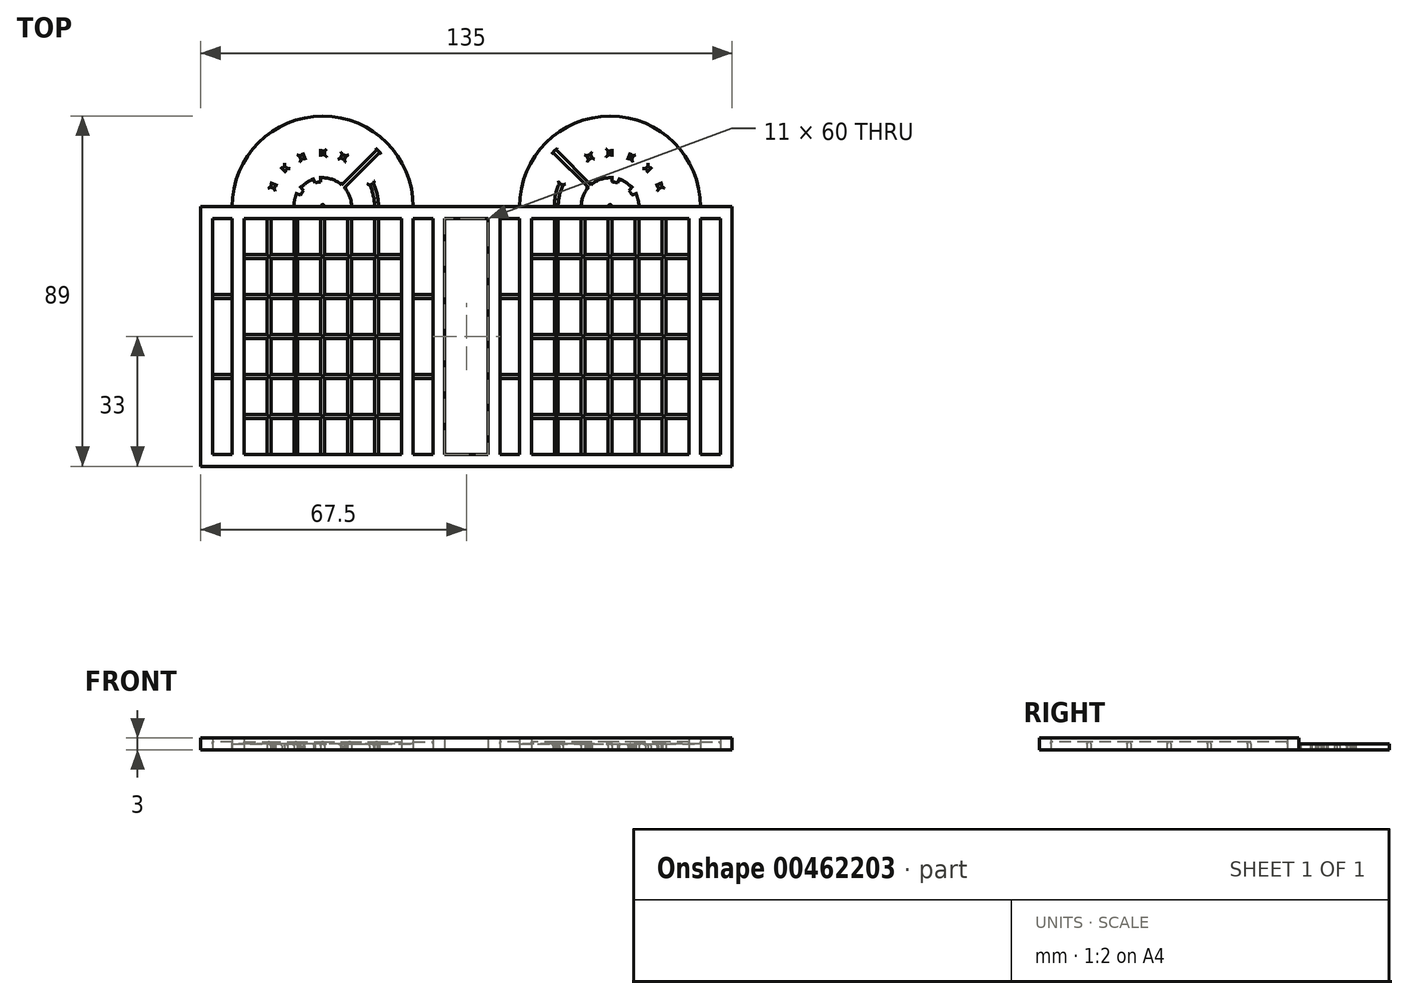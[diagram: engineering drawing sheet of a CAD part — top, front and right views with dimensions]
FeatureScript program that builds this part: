
annotation { "Feature Type Name" : "Feature", "Feature Type Description" : "" }
export const myFeature = defineFeature(function(context is Context, id is Id, definition is map)
    precondition{}
    {
        {
            var Q0;
            Q0=qCreatedBy(makeId("Top.planeOp"),FACE);
            var sketch = newSketch(context, id + "F0", { "sketchPlane" : qUnion([Q0])});
            skLineSegment(sketch, "E0.bottom", {"start": v(0, 0) * mm, "end": v(62, 0) * mm});
            skLineSegment(sketch, "E0.top", {"start": v(0, 60) * mm, "end": v(62, 60) * mm});
            skLineSegment(sketch, "E0.left", {"start": v(0, 0) * mm, "end": v(0, 60) * mm});
            skLineSegment(sketch, "E0.right", {"start": v(62, 0) * mm, "end": v(62, 60) * mm});
            skLineSegment(sketch, "E1", {"start": v(0, 0) * mm, "end": v(8, 0) * mm, "construction": true});
            skLineSegment(sketch, "E2", {"start": v(62, 0) * mm, "end": v(54, 0) * mm, "construction": true});
            skLineSegment(sketch, "E3", {"start": v(62, 0) * mm, "end": v(59, 0) * mm, "construction": true});
            skLineSegment(sketch, "E4", {"start": v(59, 0) * mm, "end": v(59, 60) * mm});
            skLineSegment(sketch, "E5", {"start": v(0, 60) * mm, "end": v(3, 60) * mm, "construction": true});
            skLineSegment(sketch, "E6", {"start": v(3, 60) * mm, "end": v(3, 0) * mm});
            skLineSegment(sketch, "E7", {"start": v(8, 0) * mm, "end": v(8, 60) * mm});
            skLineSegment(sketch, "E8", {"start": v(54, 0) * mm, "end": v(54, 60) * mm});
            skLineSegment(sketch, "E9", {"start": v(8, 0) * mm, "end": v(11, 0) * mm, "construction": true});
            skLineSegment(sketch, "E10", {"start": v(54, 0) * mm, "end": v(51, 0) * mm, "construction": true});
            skLineSegment(sketch, "E11", {"start": v(11, 0) * mm, "end": v(11, 60) * mm});
            skLineSegment(sketch, "E12", {"start": v(51, 0) * mm, "end": v(51, 60) * mm});
            skLineSegment(sketch, "E13.bottom", {"start": v(51, 0) * mm, "end": v(45.17, 0) * mm});
            skLineSegment(sketch, "E13.top", {"start": v(51, 9.17) * mm, "end": v(45.17, 9.17) * mm});
            skLineSegment(sketch, "E13.left", {"start": v(51, 0) * mm, "end": v(51, 9.17) * mm});
            skLineSegment(sketch, "E13.right", {"start": v(45.17, 0) * mm, "end": v(45.17, 9.17) * mm});
            skLineSegment(sketch, "E14.bottom", {"start": v(45.17, 0) * mm, "end": v(44.17, 0) * mm});
            skLineSegment(sketch, "E14.top", {"start": v(45.17, 9.17) * mm, "end": v(44.17, 9.17) * mm, "construction": true});
            skLineSegment(sketch, "E14.right", {"start": v(44.17, 0) * mm, "end": v(44.17, 9.17) * mm});
            skLineSegment(sketch, "E15.top", {"start": v(51, 10.17) * mm, "end": v(45.17, 10.17) * mm});
            skLineSegment(sketch, "E15.left", {"start": v(51, 9.17) * mm, "end": v(51, 10.17) * mm});
            skLineSegment(sketch, "E15.right", {"start": v(45.17, 9.17) * mm, "end": v(45.17, 10.17) * mm, "construction": true});
            skLineSegment(sketch, "E16", {"start": v(44.17, 9.17) * mm, "end": v(44.17, 10.17) * mm, "construction": true});
            skLineSegment(sketch, "E17", {"start": v(44.17, 10.17) * mm, "end": v(45.17, 10.17) * mm, "construction": true});
            skLineSegment(sketch, "E18.0.1.0", {"start": v(44.17, 20.33) * mm, "end": v(45.17, 20.33) * mm, "construction": true});
            skLineSegment(sketch, "E18.0.1.1", {"start": v(51, 20.33) * mm, "end": v(45.17, 20.33) * mm});
            skLineSegment(sketch, "E18.0.1.2", {"start": v(51, 19.33) * mm, "end": v(45.17, 19.33) * mm});
            skLineSegment(sketch, "E18.0.1.3", {"start": v(45.17, 10.17) * mm, "end": v(45.17, 19.33) * mm});
            skLineSegment(sketch, "E18.0.1.4", {"start": v(44.17, 10.17) * mm, "end": v(44.17, 19.33) * mm});
            skLineSegment(sketch, "E18.0.1.5", {"start": v(45.17, 19.33) * mm, "end": v(44.17, 19.33) * mm, "construction": true});
            skLineSegment(sketch, "E18.0.1.6", {"start": v(44.17, 19.33) * mm, "end": v(44.17, 20.33) * mm, "construction": true});
            skLineSegment(sketch, "E18.0.1.7", {"start": v(45.17, 19.33) * mm, "end": v(45.17, 20.33) * mm, "construction": true});
            skLineSegment(sketch, "E18.0.2.0", {"start": v(44.17, 30.5) * mm, "end": v(45.17, 30.5) * mm, "construction": true});
            skLineSegment(sketch, "E18.0.2.1", {"start": v(51, 30.5) * mm, "end": v(45.17, 30.5) * mm});
            skLineSegment(sketch, "E18.0.2.2", {"start": v(51, 29.5) * mm, "end": v(45.17, 29.5) * mm});
            skLineSegment(sketch, "E18.0.2.3", {"start": v(45.17, 20.33) * mm, "end": v(45.17, 29.5) * mm});
            skLineSegment(sketch, "E18.0.2.4", {"start": v(44.17, 20.33) * mm, "end": v(44.17, 29.5) * mm});
            skLineSegment(sketch, "E18.0.2.5", {"start": v(45.17, 29.5) * mm, "end": v(44.17, 29.5) * mm, "construction": true});
            skLineSegment(sketch, "E18.0.2.6", {"start": v(44.17, 29.5) * mm, "end": v(44.17, 30.5) * mm, "construction": true});
            skLineSegment(sketch, "E18.0.2.7", {"start": v(45.17, 29.5) * mm, "end": v(45.17, 30.5) * mm, "construction": true});
            skLineSegment(sketch, "E18.0.3.0", {"start": v(44.17, 40.67) * mm, "end": v(45.17, 40.67) * mm, "construction": true});
            skLineSegment(sketch, "E18.0.3.1", {"start": v(51, 40.67) * mm, "end": v(45.17, 40.67) * mm});
            skLineSegment(sketch, "E18.0.3.2", {"start": v(51, 39.67) * mm, "end": v(45.17, 39.67) * mm});
            skLineSegment(sketch, "E18.0.3.3", {"start": v(45.17, 30.5) * mm, "end": v(45.17, 39.67) * mm});
            skLineSegment(sketch, "E18.0.3.4", {"start": v(44.17, 30.5) * mm, "end": v(44.17, 39.67) * mm});
            skLineSegment(sketch, "E18.0.3.5", {"start": v(45.17, 39.67) * mm, "end": v(44.17, 39.67) * mm, "construction": true});
            skLineSegment(sketch, "E18.0.3.6", {"start": v(44.17, 39.67) * mm, "end": v(44.17, 40.67) * mm, "construction": true});
            skLineSegment(sketch, "E18.0.3.7", {"start": v(45.17, 39.67) * mm, "end": v(45.17, 40.67) * mm, "construction": true});
            skLineSegment(sketch, "E18.0.4.0", {"start": v(44.17, 50.83) * mm, "end": v(45.17, 50.83) * mm, "construction": true});
            skLineSegment(sketch, "E18.0.4.1", {"start": v(51, 50.83) * mm, "end": v(45.17, 50.83) * mm});
            skLineSegment(sketch, "E18.0.4.2", {"start": v(51, 49.83) * mm, "end": v(45.17, 49.83) * mm});
            skLineSegment(sketch, "E18.0.4.3", {"start": v(45.17, 40.67) * mm, "end": v(45.17, 49.83) * mm});
            skLineSegment(sketch, "E18.0.4.4", {"start": v(44.17, 40.67) * mm, "end": v(44.17, 49.83) * mm});
            skLineSegment(sketch, "E18.0.4.5", {"start": v(45.17, 49.83) * mm, "end": v(44.17, 49.83) * mm, "construction": true});
            skLineSegment(sketch, "E18.0.4.6", {"start": v(44.17, 49.83) * mm, "end": v(44.17, 50.83) * mm, "construction": true});
            skLineSegment(sketch, "E18.0.4.7", {"start": v(45.17, 49.83) * mm, "end": v(45.17, 50.83) * mm, "construction": true});
            skLineSegment(sketch, "E18.0.5.2", {"start": v(51, 60) * mm, "end": v(45.17, 60) * mm});
            skLineSegment(sketch, "E18.0.5.3", {"start": v(45.17, 50.83) * mm, "end": v(45.17, 60) * mm});
            skLineSegment(sketch, "E18.0.5.4", {"start": v(44.17, 50.83) * mm, "end": v(44.17, 60) * mm});
            skLineSegment(sketch, "E18.0.5.5", {"start": v(45.17, 60) * mm, "end": v(44.17, 60) * mm, "construction": true});
            skLineSegment(sketch, "E18.1.0.0", {"start": v(37.33, 10.17) * mm, "end": v(38.33, 10.17) * mm, "construction": true});
            skLineSegment(sketch, "E18.1.0.1", {"start": v(44.17, 10.17) * mm, "end": v(38.33, 10.17) * mm});
            skLineSegment(sketch, "E18.1.0.2", {"start": v(44.17, 9.17) * mm, "end": v(38.33, 9.17) * mm});
            skLineSegment(sketch, "E18.1.0.3", {"start": v(38.33, 0) * mm, "end": v(38.33, 9.17) * mm});
            skLineSegment(sketch, "E18.1.0.4", {"start": v(37.33, 0) * mm, "end": v(37.33, 9.17) * mm});
            skLineSegment(sketch, "E18.1.0.5", {"start": v(38.33, 9.17) * mm, "end": v(37.33, 9.17) * mm, "construction": true});
            skLineSegment(sketch, "E18.1.0.6", {"start": v(37.33, 9.17) * mm, "end": v(37.33, 10.17) * mm, "construction": true});
            skLineSegment(sketch, "E18.1.0.7", {"start": v(38.33, 9.17) * mm, "end": v(38.33, 10.17) * mm, "construction": true});
            skLineSegment(sketch, "E18.1.1.0", {"start": v(37.33, 20.33) * mm, "end": v(38.33, 20.33) * mm, "construction": true});
            skLineSegment(sketch, "E18.1.1.1", {"start": v(44.17, 20.33) * mm, "end": v(38.33, 20.33) * mm});
            skLineSegment(sketch, "E18.1.1.2", {"start": v(44.17, 19.33) * mm, "end": v(38.33, 19.33) * mm});
            skLineSegment(sketch, "E18.1.1.3", {"start": v(38.33, 10.17) * mm, "end": v(38.33, 19.33) * mm});
            skLineSegment(sketch, "E18.1.1.4", {"start": v(37.33, 10.17) * mm, "end": v(37.33, 19.33) * mm});
            skLineSegment(sketch, "E18.1.1.5", {"start": v(38.33, 19.33) * mm, "end": v(37.33, 19.33) * mm, "construction": true});
            skLineSegment(sketch, "E18.1.1.6", {"start": v(37.33, 19.33) * mm, "end": v(37.33, 20.33) * mm, "construction": true});
            skLineSegment(sketch, "E18.1.1.7", {"start": v(38.33, 19.33) * mm, "end": v(38.33, 20.33) * mm, "construction": true});
            skLineSegment(sketch, "E18.1.2.0", {"start": v(37.33, 30.5) * mm, "end": v(38.33, 30.5) * mm, "construction": true});
            skLineSegment(sketch, "E18.1.2.1", {"start": v(44.17, 30.5) * mm, "end": v(38.33, 30.5) * mm});
            skLineSegment(sketch, "E18.1.2.2", {"start": v(44.17, 29.5) * mm, "end": v(38.33, 29.5) * mm});
            skLineSegment(sketch, "E18.1.2.3", {"start": v(38.33, 20.33) * mm, "end": v(38.33, 29.5) * mm});
            skLineSegment(sketch, "E18.1.2.4", {"start": v(37.33, 20.33) * mm, "end": v(37.33, 29.5) * mm});
            skLineSegment(sketch, "E18.1.2.5", {"start": v(38.33, 29.5) * mm, "end": v(37.33, 29.5) * mm, "construction": true});
            skLineSegment(sketch, "E18.1.2.6", {"start": v(37.33, 29.5) * mm, "end": v(37.33, 30.5) * mm, "construction": true});
            skLineSegment(sketch, "E18.1.2.7", {"start": v(38.33, 29.5) * mm, "end": v(38.33, 30.5) * mm, "construction": true});
            skLineSegment(sketch, "E18.1.3.0", {"start": v(37.33, 40.67) * mm, "end": v(38.33, 40.67) * mm, "construction": true});
            skLineSegment(sketch, "E18.1.3.1", {"start": v(44.17, 40.67) * mm, "end": v(38.33, 40.67) * mm});
            skLineSegment(sketch, "E18.1.3.2", {"start": v(44.17, 39.67) * mm, "end": v(38.33, 39.67) * mm});
            skLineSegment(sketch, "E18.1.3.3", {"start": v(38.33, 30.5) * mm, "end": v(38.33, 39.67) * mm});
            skLineSegment(sketch, "E18.1.3.4", {"start": v(37.33, 30.5) * mm, "end": v(37.33, 39.67) * mm});
            skLineSegment(sketch, "E18.1.3.5", {"start": v(38.33, 39.67) * mm, "end": v(37.33, 39.67) * mm, "construction": true});
            skLineSegment(sketch, "E18.1.3.6", {"start": v(37.33, 39.67) * mm, "end": v(37.33, 40.67) * mm, "construction": true});
            skLineSegment(sketch, "E18.1.3.7", {"start": v(38.33, 39.67) * mm, "end": v(38.33, 40.67) * mm, "construction": true});
            skLineSegment(sketch, "E18.1.4.0", {"start": v(37.33, 50.83) * mm, "end": v(38.33, 50.83) * mm, "construction": true});
            skLineSegment(sketch, "E18.1.4.1", {"start": v(44.17, 50.83) * mm, "end": v(38.33, 50.83) * mm});
            skLineSegment(sketch, "E18.1.4.2", {"start": v(44.17, 49.83) * mm, "end": v(38.33, 49.83) * mm});
            skLineSegment(sketch, "E18.1.4.3", {"start": v(38.33, 40.67) * mm, "end": v(38.33, 49.83) * mm});
            skLineSegment(sketch, "E18.1.4.4", {"start": v(37.33, 40.67) * mm, "end": v(37.33, 49.83) * mm});
            skLineSegment(sketch, "E18.1.4.5", {"start": v(38.33, 49.83) * mm, "end": v(37.33, 49.83) * mm, "construction": true});
            skLineSegment(sketch, "E18.1.4.6", {"start": v(37.33, 49.83) * mm, "end": v(37.33, 50.83) * mm, "construction": true});
            skLineSegment(sketch, "E18.1.4.7", {"start": v(38.33, 49.83) * mm, "end": v(38.33, 50.83) * mm, "construction": true});
            skLineSegment(sketch, "E18.1.5.2", {"start": v(44.17, 60) * mm, "end": v(38.33, 60) * mm});
            skLineSegment(sketch, "E18.1.5.3", {"start": v(38.33, 50.83) * mm, "end": v(38.33, 60) * mm});
            skLineSegment(sketch, "E18.1.5.4", {"start": v(37.33, 50.83) * mm, "end": v(37.33, 60) * mm});
            skLineSegment(sketch, "E18.1.5.5", {"start": v(38.33, 60) * mm, "end": v(37.33, 60) * mm, "construction": true});
            skLineSegment(sketch, "E18.2.0.0", {"start": v(30.5, 10.17) * mm, "end": v(31.5, 10.17) * mm, "construction": true});
            skLineSegment(sketch, "E18.2.0.1", {"start": v(37.33, 10.17) * mm, "end": v(31.5, 10.17) * mm});
            skLineSegment(sketch, "E18.2.0.2", {"start": v(37.33, 9.17) * mm, "end": v(31.5, 9.17) * mm});
            skLineSegment(sketch, "E18.2.0.3", {"start": v(31.5, 0) * mm, "end": v(31.5, 9.17) * mm});
            skLineSegment(sketch, "E18.2.0.4", {"start": v(30.5, 0) * mm, "end": v(30.5, 9.17) * mm});
            skLineSegment(sketch, "E18.2.0.5", {"start": v(31.5, 9.17) * mm, "end": v(30.5, 9.17) * mm, "construction": true});
            skLineSegment(sketch, "E18.2.0.6", {"start": v(30.5, 9.17) * mm, "end": v(30.5, 10.17) * mm, "construction": true});
            skLineSegment(sketch, "E18.2.0.7", {"start": v(31.5, 9.17) * mm, "end": v(31.5, 10.17) * mm, "construction": true});
            skLineSegment(sketch, "E18.2.1.0", {"start": v(30.5, 20.33) * mm, "end": v(31.5, 20.33) * mm, "construction": true});
            skLineSegment(sketch, "E18.2.1.1", {"start": v(37.33, 20.33) * mm, "end": v(31.5, 20.33) * mm});
            skLineSegment(sketch, "E18.2.1.2", {"start": v(37.33, 19.33) * mm, "end": v(31.5, 19.33) * mm});
            skLineSegment(sketch, "E18.2.1.3", {"start": v(31.5, 10.17) * mm, "end": v(31.5, 19.33) * mm});
            skLineSegment(sketch, "E18.2.1.4", {"start": v(30.5, 10.17) * mm, "end": v(30.5, 19.33) * mm});
            skLineSegment(sketch, "E18.2.1.5", {"start": v(31.5, 19.33) * mm, "end": v(30.5, 19.33) * mm, "construction": true});
            skLineSegment(sketch, "E18.2.1.6", {"start": v(30.5, 19.33) * mm, "end": v(30.5, 20.33) * mm, "construction": true});
            skLineSegment(sketch, "E18.2.1.7", {"start": v(31.5, 19.33) * mm, "end": v(31.5, 20.33) * mm, "construction": true});
            skLineSegment(sketch, "E18.2.2.0", {"start": v(30.5, 30.5) * mm, "end": v(31.5, 30.5) * mm, "construction": true});
            skLineSegment(sketch, "E18.2.2.1", {"start": v(37.33, 30.5) * mm, "end": v(31.5, 30.5) * mm});
            skLineSegment(sketch, "E18.2.2.2", {"start": v(37.33, 29.5) * mm, "end": v(31.5, 29.5) * mm});
            skLineSegment(sketch, "E18.2.2.3", {"start": v(31.5, 20.33) * mm, "end": v(31.5, 29.5) * mm});
            skLineSegment(sketch, "E18.2.2.4", {"start": v(30.5, 20.33) * mm, "end": v(30.5, 29.5) * mm});
            skLineSegment(sketch, "E18.2.2.5", {"start": v(31.5, 29.5) * mm, "end": v(30.5, 29.5) * mm, "construction": true});
            skLineSegment(sketch, "E18.2.2.6", {"start": v(30.5, 29.5) * mm, "end": v(30.5, 30.5) * mm, "construction": true});
            skLineSegment(sketch, "E18.2.2.7", {"start": v(31.5, 29.5) * mm, "end": v(31.5, 30.5) * mm, "construction": true});
            skLineSegment(sketch, "E18.2.3.0", {"start": v(30.5, 40.67) * mm, "end": v(31.5, 40.67) * mm, "construction": true});
            skLineSegment(sketch, "E18.2.3.1", {"start": v(37.33, 40.67) * mm, "end": v(31.5, 40.67) * mm});
            skLineSegment(sketch, "E18.2.3.2", {"start": v(37.33, 39.67) * mm, "end": v(31.5, 39.67) * mm});
            skLineSegment(sketch, "E18.2.3.3", {"start": v(31.5, 30.5) * mm, "end": v(31.5, 39.67) * mm});
            skLineSegment(sketch, "E18.2.3.4", {"start": v(30.5, 30.5) * mm, "end": v(30.5, 39.67) * mm});
            skLineSegment(sketch, "E18.2.3.5", {"start": v(31.5, 39.67) * mm, "end": v(30.5, 39.67) * mm, "construction": true});
            skLineSegment(sketch, "E18.2.3.6", {"start": v(30.5, 39.67) * mm, "end": v(30.5, 40.67) * mm, "construction": true});
            skLineSegment(sketch, "E18.2.3.7", {"start": v(31.5, 39.67) * mm, "end": v(31.5, 40.67) * mm, "construction": true});
            skLineSegment(sketch, "E18.2.4.0", {"start": v(30.5, 50.83) * mm, "end": v(31.5, 50.83) * mm, "construction": true});
            skLineSegment(sketch, "E18.2.4.1", {"start": v(37.33, 50.83) * mm, "end": v(31.5, 50.83) * mm});
            skLineSegment(sketch, "E18.2.4.2", {"start": v(37.33, 49.83) * mm, "end": v(31.5, 49.83) * mm});
            skLineSegment(sketch, "E18.2.4.3", {"start": v(31.5, 40.67) * mm, "end": v(31.5, 49.83) * mm});
            skLineSegment(sketch, "E18.2.4.4", {"start": v(30.5, 40.67) * mm, "end": v(30.5, 49.83) * mm});
            skLineSegment(sketch, "E18.2.4.5", {"start": v(31.5, 49.83) * mm, "end": v(30.5, 49.83) * mm, "construction": true});
            skLineSegment(sketch, "E18.2.4.6", {"start": v(30.5, 49.83) * mm, "end": v(30.5, 50.83) * mm, "construction": true});
            skLineSegment(sketch, "E18.2.4.7", {"start": v(31.5, 49.83) * mm, "end": v(31.5, 50.83) * mm, "construction": true});
            skLineSegment(sketch, "E18.2.5.2", {"start": v(37.33, 60) * mm, "end": v(31.5, 60) * mm});
            skLineSegment(sketch, "E18.2.5.3", {"start": v(31.5, 50.83) * mm, "end": v(31.5, 60) * mm});
            skLineSegment(sketch, "E18.2.5.4", {"start": v(30.5, 50.83) * mm, "end": v(30.5, 60) * mm});
            skLineSegment(sketch, "E18.2.5.5", {"start": v(31.5, 60) * mm, "end": v(30.5, 60) * mm, "construction": true});
            skLineSegment(sketch, "E18.3.0.0", {"start": v(23.67, 10.17) * mm, "end": v(24.67, 10.17) * mm, "construction": true});
            skLineSegment(sketch, "E18.3.0.1", {"start": v(30.5, 10.17) * mm, "end": v(24.67, 10.17) * mm});
            skLineSegment(sketch, "E18.3.0.2", {"start": v(30.5, 9.17) * mm, "end": v(24.67, 9.17) * mm});
            skLineSegment(sketch, "E18.3.0.3", {"start": v(24.67, 0) * mm, "end": v(24.67, 9.17) * mm});
            skLineSegment(sketch, "E18.3.0.4", {"start": v(23.67, 0) * mm, "end": v(23.67, 9.17) * mm});
            skLineSegment(sketch, "E18.3.0.5", {"start": v(24.67, 9.17) * mm, "end": v(23.67, 9.17) * mm, "construction": true});
            skLineSegment(sketch, "E18.3.0.6", {"start": v(23.67, 9.17) * mm, "end": v(23.67, 10.17) * mm, "construction": true});
            skLineSegment(sketch, "E18.3.0.7", {"start": v(24.67, 9.17) * mm, "end": v(24.67, 10.17) * mm, "construction": true});
            skLineSegment(sketch, "E18.3.1.0", {"start": v(23.67, 20.33) * mm, "end": v(24.67, 20.33) * mm, "construction": true});
            skLineSegment(sketch, "E18.3.1.1", {"start": v(30.5, 20.33) * mm, "end": v(24.67, 20.33) * mm});
            skLineSegment(sketch, "E18.3.1.2", {"start": v(30.5, 19.33) * mm, "end": v(24.67, 19.33) * mm});
            skLineSegment(sketch, "E18.3.1.3", {"start": v(24.67, 10.17) * mm, "end": v(24.67, 19.33) * mm});
            skLineSegment(sketch, "E18.3.1.4", {"start": v(23.67, 10.17) * mm, "end": v(23.67, 19.33) * mm});
            skLineSegment(sketch, "E18.3.1.5", {"start": v(24.67, 19.33) * mm, "end": v(23.67, 19.33) * mm, "construction": true});
            skLineSegment(sketch, "E18.3.1.6", {"start": v(23.67, 19.33) * mm, "end": v(23.67, 20.33) * mm, "construction": true});
            skLineSegment(sketch, "E18.3.1.7", {"start": v(24.67, 19.33) * mm, "end": v(24.67, 20.33) * mm, "construction": true});
            skLineSegment(sketch, "E18.3.2.0", {"start": v(23.67, 30.5) * mm, "end": v(24.67, 30.5) * mm, "construction": true});
            skLineSegment(sketch, "E18.3.2.1", {"start": v(30.5, 30.5) * mm, "end": v(24.67, 30.5) * mm});
            skLineSegment(sketch, "E18.3.2.2", {"start": v(30.5, 29.5) * mm, "end": v(24.67, 29.5) * mm});
            skLineSegment(sketch, "E18.3.2.3", {"start": v(24.67, 20.33) * mm, "end": v(24.67, 29.5) * mm});
            skLineSegment(sketch, "E18.3.2.4", {"start": v(23.67, 20.33) * mm, "end": v(23.67, 29.5) * mm});
            skLineSegment(sketch, "E18.3.2.5", {"start": v(24.67, 29.5) * mm, "end": v(23.67, 29.5) * mm, "construction": true});
            skLineSegment(sketch, "E18.3.2.6", {"start": v(23.67, 29.5) * mm, "end": v(23.67, 30.5) * mm, "construction": true});
            skLineSegment(sketch, "E18.3.2.7", {"start": v(24.67, 29.5) * mm, "end": v(24.67, 30.5) * mm, "construction": true});
            skLineSegment(sketch, "E18.3.3.0", {"start": v(23.67, 40.67) * mm, "end": v(24.67, 40.67) * mm, "construction": true});
            skLineSegment(sketch, "E18.3.3.1", {"start": v(30.5, 40.67) * mm, "end": v(24.67, 40.67) * mm});
            skLineSegment(sketch, "E18.3.3.2", {"start": v(30.5, 39.67) * mm, "end": v(24.67, 39.67) * mm});
            skLineSegment(sketch, "E18.3.3.3", {"start": v(24.67, 30.5) * mm, "end": v(24.67, 39.67) * mm});
            skLineSegment(sketch, "E18.3.3.4", {"start": v(23.67, 30.5) * mm, "end": v(23.67, 39.67) * mm});
            skLineSegment(sketch, "E18.3.3.5", {"start": v(24.67, 39.67) * mm, "end": v(23.67, 39.67) * mm, "construction": true});
            skLineSegment(sketch, "E18.3.3.6", {"start": v(23.67, 39.67) * mm, "end": v(23.67, 40.67) * mm, "construction": true});
            skLineSegment(sketch, "E18.3.3.7", {"start": v(24.67, 39.67) * mm, "end": v(24.67, 40.67) * mm, "construction": true});
            skLineSegment(sketch, "E18.3.4.0", {"start": v(23.67, 50.83) * mm, "end": v(24.67, 50.83) * mm, "construction": true});
            skLineSegment(sketch, "E18.3.4.1", {"start": v(30.5, 50.83) * mm, "end": v(24.67, 50.83) * mm});
            skLineSegment(sketch, "E18.3.4.2", {"start": v(30.5, 49.83) * mm, "end": v(24.67, 49.83) * mm});
            skLineSegment(sketch, "E18.3.4.3", {"start": v(24.67, 40.67) * mm, "end": v(24.67, 49.83) * mm});
            skLineSegment(sketch, "E18.3.4.4", {"start": v(23.67, 40.67) * mm, "end": v(23.67, 49.83) * mm});
            skLineSegment(sketch, "E18.3.4.5", {"start": v(24.67, 49.83) * mm, "end": v(23.67, 49.83) * mm, "construction": true});
            skLineSegment(sketch, "E18.3.4.6", {"start": v(23.67, 49.83) * mm, "end": v(23.67, 50.83) * mm, "construction": true});
            skLineSegment(sketch, "E18.3.4.7", {"start": v(24.67, 49.83) * mm, "end": v(24.67, 50.83) * mm, "construction": true});
            skLineSegment(sketch, "E18.3.5.2", {"start": v(30.5, 60) * mm, "end": v(24.67, 60) * mm});
            skLineSegment(sketch, "E18.3.5.3", {"start": v(24.67, 50.83) * mm, "end": v(24.67, 60) * mm});
            skLineSegment(sketch, "E18.3.5.4", {"start": v(23.67, 50.83) * mm, "end": v(23.67, 60) * mm});
            skLineSegment(sketch, "E18.3.5.5", {"start": v(24.67, 60) * mm, "end": v(23.67, 60) * mm, "construction": true});
            skLineSegment(sketch, "E18.4.0.0", {"start": v(16.83, 10.17) * mm, "end": v(17.83, 10.17) * mm, "construction": true});
            skLineSegment(sketch, "E18.4.0.1", {"start": v(23.67, 10.17) * mm, "end": v(17.83, 10.17) * mm});
            skLineSegment(sketch, "E18.4.0.2", {"start": v(23.67, 9.17) * mm, "end": v(17.83, 9.17) * mm});
            skLineSegment(sketch, "E18.4.0.3", {"start": v(17.83, 0) * mm, "end": v(17.83, 9.17) * mm});
            skLineSegment(sketch, "E18.4.0.4", {"start": v(16.83, 0) * mm, "end": v(16.83, 9.17) * mm});
            skLineSegment(sketch, "E18.4.0.5", {"start": v(17.83, 9.17) * mm, "end": v(16.83, 9.17) * mm, "construction": true});
            skLineSegment(sketch, "E18.4.0.6", {"start": v(16.83, 9.17) * mm, "end": v(16.83, 10.17) * mm, "construction": true});
            skLineSegment(sketch, "E18.4.0.7", {"start": v(17.83, 9.17) * mm, "end": v(17.83, 10.17) * mm, "construction": true});
            skLineSegment(sketch, "E18.4.1.0", {"start": v(16.83, 20.33) * mm, "end": v(17.83, 20.33) * mm, "construction": true});
            skLineSegment(sketch, "E18.4.1.1", {"start": v(23.67, 20.33) * mm, "end": v(17.83, 20.33) * mm});
            skLineSegment(sketch, "E18.4.1.2", {"start": v(23.67, 19.33) * mm, "end": v(17.83, 19.33) * mm});
            skLineSegment(sketch, "E18.4.1.3", {"start": v(17.83, 10.17) * mm, "end": v(17.83, 19.33) * mm});
            skLineSegment(sketch, "E18.4.1.4", {"start": v(16.83, 10.17) * mm, "end": v(16.83, 19.33) * mm});
            skLineSegment(sketch, "E18.4.1.5", {"start": v(17.83, 19.33) * mm, "end": v(16.83, 19.33) * mm, "construction": true});
            skLineSegment(sketch, "E18.4.1.6", {"start": v(16.83, 19.33) * mm, "end": v(16.83, 20.33) * mm, "construction": true});
            skLineSegment(sketch, "E18.4.1.7", {"start": v(17.83, 19.33) * mm, "end": v(17.83, 20.33) * mm, "construction": true});
            skLineSegment(sketch, "E18.4.2.0", {"start": v(16.83, 30.5) * mm, "end": v(17.83, 30.5) * mm, "construction": true});
            skLineSegment(sketch, "E18.4.2.1", {"start": v(23.67, 30.5) * mm, "end": v(17.83, 30.5) * mm});
            skLineSegment(sketch, "E18.4.2.2", {"start": v(23.67, 29.5) * mm, "end": v(17.83, 29.5) * mm});
            skLineSegment(sketch, "E18.4.2.3", {"start": v(17.83, 20.33) * mm, "end": v(17.83, 29.5) * mm});
            skLineSegment(sketch, "E18.4.2.4", {"start": v(16.83, 20.33) * mm, "end": v(16.83, 29.5) * mm});
            skLineSegment(sketch, "E18.4.2.5", {"start": v(17.83, 29.5) * mm, "end": v(16.83, 29.5) * mm, "construction": true});
            skLineSegment(sketch, "E18.4.2.6", {"start": v(16.83, 29.5) * mm, "end": v(16.83, 30.5) * mm, "construction": true});
            skLineSegment(sketch, "E18.4.2.7", {"start": v(17.83, 29.5) * mm, "end": v(17.83, 30.5) * mm, "construction": true});
            skLineSegment(sketch, "E18.4.3.0", {"start": v(16.83, 40.67) * mm, "end": v(17.83, 40.67) * mm, "construction": true});
            skLineSegment(sketch, "E18.4.3.1", {"start": v(23.67, 40.67) * mm, "end": v(17.83, 40.67) * mm});
            skLineSegment(sketch, "E18.4.3.2", {"start": v(23.67, 39.67) * mm, "end": v(17.83, 39.67) * mm});
            skLineSegment(sketch, "E18.4.3.3", {"start": v(17.83, 30.5) * mm, "end": v(17.83, 39.67) * mm});
            skLineSegment(sketch, "E18.4.3.4", {"start": v(16.83, 30.5) * mm, "end": v(16.83, 39.67) * mm});
            skLineSegment(sketch, "E18.4.3.5", {"start": v(17.83, 39.67) * mm, "end": v(16.83, 39.67) * mm, "construction": true});
            skLineSegment(sketch, "E18.4.3.6", {"start": v(16.83, 39.67) * mm, "end": v(16.83, 40.67) * mm, "construction": true});
            skLineSegment(sketch, "E18.4.3.7", {"start": v(17.83, 39.67) * mm, "end": v(17.83, 40.67) * mm, "construction": true});
            skLineSegment(sketch, "E18.4.4.0", {"start": v(16.83, 50.83) * mm, "end": v(17.83, 50.83) * mm, "construction": true});
            skLineSegment(sketch, "E18.4.4.1", {"start": v(23.67, 50.83) * mm, "end": v(17.83, 50.83) * mm});
            skLineSegment(sketch, "E18.4.4.2", {"start": v(23.67, 49.83) * mm, "end": v(17.83, 49.83) * mm});
            skLineSegment(sketch, "E18.4.4.3", {"start": v(17.83, 40.67) * mm, "end": v(17.83, 49.83) * mm});
            skLineSegment(sketch, "E18.4.4.4", {"start": v(16.83, 40.67) * mm, "end": v(16.83, 49.83) * mm});
            skLineSegment(sketch, "E18.4.4.5", {"start": v(17.83, 49.83) * mm, "end": v(16.83, 49.83) * mm, "construction": true});
            skLineSegment(sketch, "E18.4.4.6", {"start": v(16.83, 49.83) * mm, "end": v(16.83, 50.83) * mm, "construction": true});
            skLineSegment(sketch, "E18.4.4.7", {"start": v(17.83, 49.83) * mm, "end": v(17.83, 50.83) * mm, "construction": true});
            skLineSegment(sketch, "E18.4.5.2", {"start": v(23.67, 60) * mm, "end": v(17.83, 60) * mm});
            skLineSegment(sketch, "E18.4.5.3", {"start": v(17.83, 50.83) * mm, "end": v(17.83, 60) * mm});
            skLineSegment(sketch, "E18.4.5.4", {"start": v(16.83, 50.83) * mm, "end": v(16.83, 60) * mm});
            skLineSegment(sketch, "E18.4.5.5", {"start": v(17.83, 60) * mm, "end": v(16.83, 60) * mm, "construction": true});
            skLineSegment(sketch, "E18.5.0.1", {"start": v(16.83, 10.17) * mm, "end": v(11, 10.17) * mm});
            skLineSegment(sketch, "E18.5.0.2", {"start": v(16.83, 9.17) * mm, "end": v(11, 9.17) * mm});
            skLineSegment(sketch, "E18.5.0.3", {"start": v(11, 0) * mm, "end": v(11, 9.17) * mm});
            skLineSegment(sketch, "E18.5.0.7", {"start": v(11, 9.17) * mm, "end": v(11, 10.17) * mm, "construction": true});
            skLineSegment(sketch, "E18.5.1.1", {"start": v(16.83, 20.33) * mm, "end": v(11, 20.33) * mm});
            skLineSegment(sketch, "E18.5.1.2", {"start": v(16.83, 19.33) * mm, "end": v(11, 19.33) * mm});
            skLineSegment(sketch, "E18.5.1.3", {"start": v(11, 10.17) * mm, "end": v(11, 19.33) * mm});
            skLineSegment(sketch, "E18.5.1.7", {"start": v(11, 19.33) * mm, "end": v(11, 20.33) * mm, "construction": true});
            skLineSegment(sketch, "E18.5.2.1", {"start": v(16.83, 30.5) * mm, "end": v(11, 30.5) * mm});
            skLineSegment(sketch, "E18.5.2.2", {"start": v(16.83, 29.5) * mm, "end": v(11, 29.5) * mm});
            skLineSegment(sketch, "E18.5.2.3", {"start": v(11, 20.33) * mm, "end": v(11, 29.5) * mm});
            skLineSegment(sketch, "E18.5.2.7", {"start": v(11, 29.5) * mm, "end": v(11, 30.5) * mm, "construction": true});
            skLineSegment(sketch, "E18.5.3.1", {"start": v(16.83, 40.67) * mm, "end": v(11, 40.67) * mm});
            skLineSegment(sketch, "E18.5.3.2", {"start": v(16.83, 39.67) * mm, "end": v(11, 39.67) * mm});
            skLineSegment(sketch, "E18.5.3.3", {"start": v(11, 30.5) * mm, "end": v(11, 39.67) * mm});
            skLineSegment(sketch, "E18.5.3.7", {"start": v(11, 39.67) * mm, "end": v(11, 40.67) * mm, "construction": true});
            skLineSegment(sketch, "E18.5.4.1", {"start": v(16.83, 50.83) * mm, "end": v(11, 50.83) * mm});
            skLineSegment(sketch, "E18.5.4.2", {"start": v(16.83, 49.83) * mm, "end": v(11, 49.83) * mm});
            skLineSegment(sketch, "E18.5.4.3", {"start": v(11, 40.67) * mm, "end": v(11, 49.83) * mm});
            skLineSegment(sketch, "E18.5.4.7", {"start": v(11, 49.83) * mm, "end": v(11, 50.83) * mm, "construction": true});
            skLineSegment(sketch, "E18.5.5.2", {"start": v(16.83, 60) * mm, "end": v(11, 60) * mm});
            skLineSegment(sketch, "E18.5.5.3", {"start": v(11, 50.83) * mm, "end": v(11, 60) * mm});
            skLineSegment(sketch, "E18.direction1", {"start": v(44.17, 0) * mm, "end": v(37.33, 0) * mm, "construction": true});
            skLineSegment(sketch, "E18.direction2", {"start": v(44.17, 0) * mm, "end": v(44.17, 10.17) * mm, "construction": true});
            skLineSegment(sketch, "E19.top", {"start": v(0, -3) * mm, "end": v(62, -3) * mm});
            skLineSegment(sketch, "E19.left", {"start": v(0, 0) * mm, "end": v(0, -3) * mm});
            skLineSegment(sketch, "E19.right", {"start": v(62, 0) * mm, "end": v(62, -3) * mm});
            skLineSegment(sketch, "E20.top", {"start": v(0, 63) * mm, "end": v(62, 63) * mm});
            skLineSegment(sketch, "E20.left", {"start": v(0, 60) * mm, "end": v(0, 63) * mm});
            skLineSegment(sketch, "E20.right", {"start": v(62, 60) * mm, "end": v(62, 63) * mm});
            skLineSegment(sketch, "E21", {"start": v(31, 63) * mm, "end": v(31, 86) * mm, "construction": true});
            skArc(sketch, "E22", {"start": v(11, 63) * mm, "mid": v(31, 83) * mm, "end": v(51, 63) * mm});
            skArc(sketch, "E23", {"start": v(8, 63) * mm, "mid": v(31, 86) * mm, "end": v(54, 63) * mm});
            skArc(sketch, "E24", {"start": v(16.83, 63) * mm, "mid": v(31, 77.17) * mm, "end": v(45.17, 63) * mm});
            skArc(sketch, "E25", {"start": v(17.83, 63) * mm, "mid": v(31, 76.17) * mm, "end": v(44.17, 63) * mm});
            skArc(sketch, "E26", {"start": v(23.67, 63) * mm, "mid": v(31, 70.33) * mm, "end": v(38.33, 63) * mm});
            skArc(sketch, "E27", {"start": v(24.67, 63) * mm, "mid": v(31, 69.33) * mm, "end": v(37.33, 63) * mm});
            skArc(sketch, "E28", {"start": v(30.5, 63) * mm, "mid": v(31, 63.5) * mm, "end": v(31.5, 63) * mm});
            skLineSegment(sketch, "E29", {"start": v(31, 63) * mm, "end": v(8, 63) * mm});
            skLineSegment(sketch, "E30.1.0", {"start": v(31, 63) * mm, "end": v(9.75, 71.8) * mm, "construction": true});
            skLineSegment(sketch, "E30.2.0", {"start": v(31, 63) * mm, "end": v(14.74, 79.26) * mm, "construction": true});
            skLineSegment(sketch, "E30.3.0", {"start": v(31, 63) * mm, "end": v(22.2, 84.25) * mm, "construction": true});
            skLineSegment(sketch, "E30.5.0", {"start": v(31, 63) * mm, "end": v(39.8, 84.25) * mm, "construction": true});
            skLineSegment(sketch, "E30.6.0", {"start": v(31, 63) * mm, "end": v(47.26, 79.26) * mm, "construction": true});
            skLineSegment(sketch, "E30.7.0", {"start": v(31, 63) * mm, "end": v(52.25, 71.8) * mm, "construction": true});
            skLineSegment(sketch, "E30.8.0", {"start": v(31, 63) * mm, "end": v(54, 63) * mm});
            skLineSegment(sketch, "E30.anchor1", {"start": v(31, 63) * mm, "end": v(8, 63) * mm, "construction": true});
            skLineSegment(sketch, "E30.anchor2", {"start": v(31, 63) * mm, "end": v(54, 63) * mm, "construction": true});
            skLineSegment(sketch, "E31.0", {"start": v(30.08, 63.92) * mm, "end": v(12.72, 71.11) * mm});
            skLineSegment(sketch, "E32.MirrorCS", {"start": v(29.7, 63) * mm, "end": v(12.34, 70.19) * mm});
            skLineSegment(sketch, "E33.0", {"start": v(30.5, 64.2) * mm, "end": v(17.22, 77.5) * mm});
            skLineSegment(sketch, "E34.MirrorCS", {"start": v(28.87, 64.42) * mm, "end": v(16.5, 76.78) * mm});
            skLineSegment(sketch, "E35.0", {"start": v(31, 64.3) * mm, "end": v(23.81, 81.66) * mm});
            skLineSegment(sketch, "E36.MirrorCS", {"start": v(30.08, 63.92) * mm, "end": v(22.89, 81.28) * mm});
            skLineSegment(sketch, "E37.0", {"start": v(31.5, 65.51) * mm, "end": v(31.5, 83) * mm});
            skLineSegment(sketch, "E38.0", {"start": v(30.5, 65.51) * mm, "end": v(30.5, 83) * mm});
            skLineSegment(sketch, "E39.0", {"start": v(32.42, 65.13) * mm, "end": v(39.11, 81.28) * mm});
            skLineSegment(sketch, "E40.0", {"start": v(31, 64.3) * mm, "end": v(38.19, 81.66) * mm});
            skLineSegment(sketch, "E41.0", {"start": v(32.3, 63) * mm, "end": v(49.66, 70.19) * mm});
            skLineSegment(sketch, "E42.0", {"start": v(33.13, 64.42) * mm, "end": v(49.28, 71.11) * mm});
            skLineSegment(sketch, "E43.0", {"start": v(33.13, 64.42) * mm, "end": v(45.5, 76.78) * mm});
            skLineSegment(sketch, "E44.0", {"start": v(32.42, 65.13) * mm, "end": v(44.78, 77.5) * mm});
            skSolve(sketch);
        }
        {
            var Q0;
            {var subQ10=sQuery(id+"F0.wireOp",EDGE,"E23");Q0=makeQuery(id+"F0.imprint","IMPRINT",FACE,{"disambiguationData":[TD([[makeQuery(id+"F0.imprint","IMPRINT",EDGE,{"derivedFrom":subQ10}),-1.0]])]});}
            var Q1;
            {var subQ22=sQuery(id+"F0.wireOp",EDGE,"E20.left");Q1=makeQuery(id+"F0.imprint","IMPRINT",FACE,{"disambiguationData":[TD([[makeQuery(id+"F0.imprint","IMPRINT",EDGE,{"derivedFrom":subQ22}),-1.0]])]});}
            var Q2;
            {var subQ0=sQuery(id+"F0.wireOp",EDGE,"E0.right");Q2=makeQuery(id+"F0.imprint","IMPRINT",FACE,{"disambiguationData":[TD([[makeQuery(id+"F0.imprint","IMPRINT",EDGE,{"derivedFrom":subQ0}),1.0]])]});}
            var Q3;
            {var subQ14=sQuery(id+"F0.wireOp",EDGE,"E7");Q3=makeQuery(id+"F0.imprint","IMPRINT",FACE,{"disambiguationData":[TD([[makeQuery(id+"F0.imprint","IMPRINT",EDGE,{"derivedFrom":subQ14}),-1.0]])]});}
            var Q4;
            {var subQ0=sQuery(id+"F0.wireOp",EDGE,"E0.left");Q4=makeQuery(id+"F0.imprint","IMPRINT",FACE,{"disambiguationData":[TD([[makeQuery(id+"F0.imprint","IMPRINT",EDGE,{"derivedFrom":subQ0}),-1.0]])]});}
            var Q5;
            {var subQ5=sQuery(id+"F0.wireOp",EDGE,"E8");Q5=makeQuery(id+"F0.imprint","IMPRINT",FACE,{"disambiguationData":[TD([[makeQuery(id+"F0.imprint","IMPRINT",EDGE,{"derivedFrom":subQ5}),1.0]])]});}
            var Q6;
            Q6=makeQuery(id+"F0.imprint","IMPRINT",FACE,{"disambiguationData":[TD([[makeQuery(id+"F0.imprint","IMPRINT",EDGE,{"derivedFrom":sQuery(id+"F0.wireOp",EDGE,"E19.top")}),1.0]])]});
            extrude(context, id + "F1", {"entities" : qUnion([Q0, Q1, Q2, Q3, Q4, Q5, Q6]), "depth" : 3 * mm, "offsetDistance" : 25 * mm});
        }
        {
            var Q0;
            {var subQ0=sQuery(id+"F0.wireOp",EDGE,"E24");var subQ1=sQuery(id+"F0.wireOp",EDGE,"E20.top");var subQ2=makeQuery(id+"F0.imprint","INTERSECT",VERTEX,{"disambiguationData":[OD(0.0)],"derivedFrom":[subQ1,subQ0]});Q0=makeQuery(id+"F0.imprint","IMPRINT",FACE,{"disambiguationData":[TD([[makeQuery(id+"F0.imprint","IMPRINT",EDGE,{"disambiguationData":[TD([[subQ2,-1.0]])],"derivedFrom":subQ1}),1.0]])]});}
            var Q1;
            {var subQ0=sQuery(id+"F0.wireOp",EDGE,"E31.0");var subQ1=sQuery(id+"F0.wireOp",EDGE,"E24");var subQ2=makeQuery(id+"F0.imprint","INTERSECT",VERTEX,{"derivedFrom":[subQ1,subQ0]});Q1=makeQuery(id+"F0.imprint","IMPRINT",FACE,{"disambiguationData":[TD([[makeQuery(id+"F0.imprint","IMPRINT",EDGE,{"disambiguationData":[TD([[subQ2,-1.0]])],"derivedFrom":subQ1}),-1.0]])]});}
            var Q2;
            {var subQ0=sQuery(id+"F0.wireOp",EDGE,"E35.0");var subQ1=sQuery(id+"F0.wireOp",EDGE,"E24");var subQ2=makeQuery(id+"F0.imprint","INTERSECT",VERTEX,{"derivedFrom":[subQ1,subQ0]});Q2=makeQuery(id+"F0.imprint","IMPRINT",FACE,{"disambiguationData":[TD([[makeQuery(id+"F0.imprint","IMPRINT",EDGE,{"disambiguationData":[TD([[subQ2,-1.0]])],"derivedFrom":subQ1}),-1.0]])]});}
            var Q3;
            {var subQ0=sQuery(id+"F0.wireOp",EDGE,"E37.0");var subQ1=sQuery(id+"F0.wireOp",EDGE,"E24");var subQ2=makeQuery(id+"F0.imprint","INTERSECT",VERTEX,{"derivedFrom":[subQ1,subQ0]});Q3=makeQuery(id+"F0.imprint","IMPRINT",FACE,{"disambiguationData":[TD([[makeQuery(id+"F0.imprint","IMPRINT",EDGE,{"disambiguationData":[TD([[subQ2,-1.0]])],"derivedFrom":subQ1}),-1.0]])]});}
            var Q4;
            {var subQ0=sQuery(id+"F0.wireOp",EDGE,"E39.0");var subQ1=sQuery(id+"F0.wireOp",EDGE,"E24");var subQ2=makeQuery(id+"F0.imprint","INTERSECT",VERTEX,{"derivedFrom":[subQ1,subQ0]});Q4=makeQuery(id+"F0.imprint","IMPRINT",FACE,{"disambiguationData":[TD([[makeQuery(id+"F0.imprint","IMPRINT",EDGE,{"disambiguationData":[TD([[subQ2,-1.0]])],"derivedFrom":subQ1}),-1.0]])]});}
            var Q5;
            {var subQ0=sQuery(id+"F0.wireOp",EDGE,"E42.0");var subQ1=sQuery(id+"F0.wireOp",EDGE,"E24");var subQ2=makeQuery(id+"F0.imprint","INTERSECT",VERTEX,{"derivedFrom":[subQ1,subQ0]});Q5=makeQuery(id+"F0.imprint","IMPRINT",FACE,{"disambiguationData":[TD([[makeQuery(id+"F0.imprint","IMPRINT",EDGE,{"disambiguationData":[TD([[subQ2,1.0]])],"derivedFrom":subQ1}),-1.0]])]});}
            var Q6;
            {var subQ0=sQuery(id+"F0.wireOp",EDGE,"E24");var subQ1=sQuery(id+"F0.wireOp",EDGE,"E20.top");var subQ2=makeQuery(id+"F0.imprint","INTERSECT",VERTEX,{"disambiguationData":[OD(1.0)],"derivedFrom":[subQ1,subQ0]});Q6=makeQuery(id+"F0.imprint","IMPRINT",FACE,{"disambiguationData":[TD([[makeQuery(id+"F0.imprint","IMPRINT",EDGE,{"disambiguationData":[TD([[subQ2,1.0]])],"derivedFrom":subQ1}),1.0]])]});}
            var Q7;
            {var subQ0=sQuery(id+"F0.wireOp",EDGE,"E34.MirrorCS");var subQ1=sQuery(id+"F0.wireOp",EDGE,"E22");var subQ2=makeQuery(id+"F0.imprint","INTERSECT",VERTEX,{"derivedFrom":[subQ1,subQ0]});Q7=makeQuery(id+"F0.imprint","IMPRINT",FACE,{"disambiguationData":[TD([[makeQuery(id+"F0.imprint","IMPRINT",EDGE,{"disambiguationData":[TD([[subQ2,-1.0]])],"derivedFrom":subQ1}),-1.0]])]});}
            var Q8;
            {var subQ0=sQuery(id+"F0.wireOp",EDGE,"E32.MirrorCS");var subQ1=sQuery(id+"F0.wireOp",EDGE,"E22");var subQ2=makeQuery(id+"F0.imprint","INTERSECT",VERTEX,{"derivedFrom":[subQ1,subQ0]});Q8=makeQuery(id+"F0.imprint","IMPRINT",FACE,{"disambiguationData":[TD([[makeQuery(id+"F0.imprint","IMPRINT",EDGE,{"disambiguationData":[TD([[subQ2,-1.0]])],"derivedFrom":subQ1}),-1.0]])]});}
            var Q9;
            {var subQ0=sQuery(id+"F0.wireOp",EDGE,"E36.MirrorCS");var subQ1=sQuery(id+"F0.wireOp",EDGE,"E22");var subQ2=makeQuery(id+"F0.imprint","INTERSECT",VERTEX,{"derivedFrom":[subQ1,subQ0]});Q9=makeQuery(id+"F0.imprint","IMPRINT",FACE,{"disambiguationData":[TD([[makeQuery(id+"F0.imprint","IMPRINT",EDGE,{"disambiguationData":[TD([[subQ2,-1.0]])],"derivedFrom":subQ1}),-1.0]])]});}
            var Q10;
            {var subQ0=sQuery(id+"F0.wireOp",EDGE,"E38.0");var subQ1=sQuery(id+"F0.wireOp",EDGE,"E22");var subQ2=makeQuery(id+"F0.imprint","INTERSECT",VERTEX,{"derivedFrom":[subQ1,subQ0]});Q10=makeQuery(id+"F0.imprint","IMPRINT",FACE,{"disambiguationData":[TD([[makeQuery(id+"F0.imprint","IMPRINT",EDGE,{"disambiguationData":[TD([[subQ2,-1.0]])],"derivedFrom":subQ1}),-1.0]])]});}
            var Q11;
            {var subQ0=sQuery(id+"F0.wireOp",EDGE,"E40.0");var subQ1=sQuery(id+"F0.wireOp",EDGE,"E22");var subQ2=makeQuery(id+"F0.imprint","INTERSECT",VERTEX,{"derivedFrom":[subQ1,subQ0]});Q11=makeQuery(id+"F0.imprint","IMPRINT",FACE,{"disambiguationData":[TD([[makeQuery(id+"F0.imprint","IMPRINT",EDGE,{"disambiguationData":[TD([[subQ2,-1.0]])],"derivedFrom":subQ1}),-1.0]])]});}
            var Q12;
            {var subQ0=sQuery(id+"F0.wireOp",EDGE,"E44.0");var subQ1=sQuery(id+"F0.wireOp",EDGE,"E22");var subQ2=makeQuery(id+"F0.imprint","INTERSECT",VERTEX,{"derivedFrom":[subQ1,subQ0]});Q12=makeQuery(id+"F0.imprint","IMPRINT",FACE,{"disambiguationData":[TD([[makeQuery(id+"F0.imprint","IMPRINT",EDGE,{"disambiguationData":[TD([[subQ2,-1.0]])],"derivedFrom":subQ1}),-1.0]])]});}
            var Q13;
            {var subQ0=sQuery(id+"F0.wireOp",EDGE,"E42.0");var subQ1=sQuery(id+"F0.wireOp",EDGE,"E22");var subQ2=makeQuery(id+"F0.imprint","INTERSECT",VERTEX,{"derivedFrom":[subQ1,subQ0]});Q13=makeQuery(id+"F0.imprint","IMPRINT",FACE,{"disambiguationData":[TD([[makeQuery(id+"F0.imprint","IMPRINT",EDGE,{"disambiguationData":[TD([[subQ2,-1.0]])],"derivedFrom":subQ1}),-1.0]])]});}
            var Q14;
            {var subQ0=sQuery(id+"F0.wireOp",EDGE,"E41.0");var subQ1=sQuery(id+"F0.wireOp",EDGE,"E24");var subQ2=makeQuery(id+"F0.imprint","INTERSECT",VERTEX,{"derivedFrom":[subQ1,subQ0]});Q14=makeQuery(id+"F0.imprint","IMPRINT",FACE,{"disambiguationData":[TD([[makeQuery(id+"F0.imprint","IMPRINT",EDGE,{"disambiguationData":[TD([[subQ2,1.0]])],"derivedFrom":subQ1}),-1.0]])]});}
            var Q15;
            {var subQ0=sQuery(id+"F0.wireOp",EDGE,"E43.0");var subQ1=sQuery(id+"F0.wireOp",EDGE,"E24");var subQ2=makeQuery(id+"F0.imprint","INTERSECT",VERTEX,{"derivedFrom":[subQ1,subQ0]});Q15=makeQuery(id+"F0.imprint","IMPRINT",FACE,{"disambiguationData":[TD([[makeQuery(id+"F0.imprint","IMPRINT",EDGE,{"disambiguationData":[TD([[subQ2,1.0]])],"derivedFrom":subQ1}),-1.0]])]});}
            var Q16;
            {var subQ0=sQuery(id+"F0.wireOp",EDGE,"E39.0");var subQ1=sQuery(id+"F0.wireOp",EDGE,"E24");var subQ2=makeQuery(id+"F0.imprint","INTERSECT",VERTEX,{"derivedFrom":[subQ1,subQ0]});Q16=makeQuery(id+"F0.imprint","IMPRINT",FACE,{"disambiguationData":[TD([[makeQuery(id+"F0.imprint","IMPRINT",EDGE,{"disambiguationData":[TD([[subQ2,1.0]])],"derivedFrom":subQ1}),-1.0]])]});}
            var Q17;
            {var subQ0=sQuery(id+"F0.wireOp",EDGE,"E37.0");var subQ1=sQuery(id+"F0.wireOp",EDGE,"E24");var subQ2=makeQuery(id+"F0.imprint","INTERSECT",VERTEX,{"derivedFrom":[subQ1,subQ0]});Q17=makeQuery(id+"F0.imprint","IMPRINT",FACE,{"disambiguationData":[TD([[makeQuery(id+"F0.imprint","IMPRINT",EDGE,{"disambiguationData":[TD([[subQ2,1.0]])],"derivedFrom":subQ1}),-1.0]])]});}
            var Q18;
            {var subQ0=sQuery(id+"F0.wireOp",EDGE,"E35.0");var subQ1=sQuery(id+"F0.wireOp",EDGE,"E24");var subQ2=makeQuery(id+"F0.imprint","INTERSECT",VERTEX,{"derivedFrom":[subQ1,subQ0]});Q18=makeQuery(id+"F0.imprint","IMPRINT",FACE,{"disambiguationData":[TD([[makeQuery(id+"F0.imprint","IMPRINT",EDGE,{"disambiguationData":[TD([[subQ2,1.0]])],"derivedFrom":subQ1}),-1.0]])]});}
            var Q19;
            {var subQ0=sQuery(id+"F0.wireOp",EDGE,"E33.0");var subQ1=sQuery(id+"F0.wireOp",EDGE,"E24");var subQ2=makeQuery(id+"F0.imprint","INTERSECT",VERTEX,{"derivedFrom":[subQ1,subQ0]});Q19=makeQuery(id+"F0.imprint","IMPRINT",FACE,{"disambiguationData":[TD([[makeQuery(id+"F0.imprint","IMPRINT",EDGE,{"disambiguationData":[TD([[subQ2,1.0]])],"derivedFrom":subQ1}),-1.0]])]});}
            var Q20;
            {var subQ0=sQuery(id+"F0.wireOp",EDGE,"E31.0");var subQ1=sQuery(id+"F0.wireOp",EDGE,"E24");var subQ2=makeQuery(id+"F0.imprint","INTERSECT",VERTEX,{"derivedFrom":[subQ1,subQ0]});Q20=makeQuery(id+"F0.imprint","IMPRINT",FACE,{"disambiguationData":[TD([[makeQuery(id+"F0.imprint","IMPRINT",EDGE,{"disambiguationData":[TD([[subQ2,1.0]])],"derivedFrom":subQ1}),-1.0]])]});}
            var Q21;
            {var subQ0=sQuery(id+"F0.wireOp",EDGE,"E32.MirrorCS");var subQ1=sQuery(id+"F0.wireOp",EDGE,"E25");var subQ2=makeQuery(id+"F0.imprint","INTERSECT",VERTEX,{"derivedFrom":[subQ1,subQ0]});Q21=makeQuery(id+"F0.imprint","IMPRINT",FACE,{"disambiguationData":[TD([[makeQuery(id+"F0.imprint","IMPRINT",EDGE,{"disambiguationData":[TD([[subQ2,-1.0]])],"derivedFrom":subQ1}),-1.0]])]});}
            var Q22;
            {var subQ0=sQuery(id+"F0.wireOp",EDGE,"E34.MirrorCS");var subQ1=sQuery(id+"F0.wireOp",EDGE,"E25");var subQ2=makeQuery(id+"F0.imprint","INTERSECT",VERTEX,{"derivedFrom":[subQ1,subQ0]});Q22=makeQuery(id+"F0.imprint","IMPRINT",FACE,{"disambiguationData":[TD([[makeQuery(id+"F0.imprint","IMPRINT",EDGE,{"disambiguationData":[TD([[subQ2,-1.0]])],"derivedFrom":subQ1}),-1.0]])]});}
            var Q23;
            {var subQ0=sQuery(id+"F0.wireOp",EDGE,"E36.MirrorCS");var subQ1=sQuery(id+"F0.wireOp",EDGE,"E25");var subQ2=makeQuery(id+"F0.imprint","INTERSECT",VERTEX,{"derivedFrom":[subQ1,subQ0]});Q23=makeQuery(id+"F0.imprint","IMPRINT",FACE,{"disambiguationData":[TD([[makeQuery(id+"F0.imprint","IMPRINT",EDGE,{"disambiguationData":[TD([[subQ2,-1.0]])],"derivedFrom":subQ1}),-1.0]])]});}
            var Q24;
            {var subQ0=sQuery(id+"F0.wireOp",EDGE,"E38.0");var subQ1=sQuery(id+"F0.wireOp",EDGE,"E25");var subQ2=makeQuery(id+"F0.imprint","INTERSECT",VERTEX,{"derivedFrom":[subQ1,subQ0]});Q24=makeQuery(id+"F0.imprint","IMPRINT",FACE,{"disambiguationData":[TD([[makeQuery(id+"F0.imprint","IMPRINT",EDGE,{"disambiguationData":[TD([[subQ2,-1.0]])],"derivedFrom":subQ1}),-1.0]])]});}
            var Q25;
            {var subQ0=sQuery(id+"F0.wireOp",EDGE,"E40.0");var subQ1=sQuery(id+"F0.wireOp",EDGE,"E25");var subQ2=makeQuery(id+"F0.imprint","INTERSECT",VERTEX,{"derivedFrom":[subQ1,subQ0]});Q25=makeQuery(id+"F0.imprint","IMPRINT",FACE,{"disambiguationData":[TD([[makeQuery(id+"F0.imprint","IMPRINT",EDGE,{"disambiguationData":[TD([[subQ2,-1.0]])],"derivedFrom":subQ1}),-1.0]])]});}
            var Q26;
            {var subQ0=sQuery(id+"F0.wireOp",EDGE,"E44.0");var subQ1=sQuery(id+"F0.wireOp",EDGE,"E25");var subQ2=makeQuery(id+"F0.imprint","INTERSECT",VERTEX,{"derivedFrom":[subQ1,subQ0]});Q26=makeQuery(id+"F0.imprint","IMPRINT",FACE,{"disambiguationData":[TD([[makeQuery(id+"F0.imprint","IMPRINT",EDGE,{"disambiguationData":[TD([[subQ2,-1.0]])],"derivedFrom":subQ1}),-1.0]])]});}
            var Q27;
            {var subQ0=sQuery(id+"F0.wireOp",EDGE,"E42.0");var subQ1=sQuery(id+"F0.wireOp",EDGE,"E25");var subQ2=makeQuery(id+"F0.imprint","INTERSECT",VERTEX,{"derivedFrom":[subQ1,subQ0]});Q27=makeQuery(id+"F0.imprint","IMPRINT",FACE,{"disambiguationData":[TD([[makeQuery(id+"F0.imprint","IMPRINT",EDGE,{"disambiguationData":[TD([[subQ2,-1.0]])],"derivedFrom":subQ1}),-1.0]])]});}
            var Q28;
            {var subQ0=sQuery(id+"F0.wireOp",EDGE,"E26");var subQ1=sQuery(id+"F0.wireOp",EDGE,"E20.top");var subQ2=makeQuery(id+"F0.imprint","INTERSECT",VERTEX,{"disambiguationData":[OD(1.0)],"derivedFrom":[subQ1,subQ0]});Q28=makeQuery(id+"F0.imprint","IMPRINT",FACE,{"disambiguationData":[TD([[makeQuery(id+"F0.imprint","IMPRINT",EDGE,{"disambiguationData":[TD([[subQ2,1.0]])],"derivedFrom":subQ1}),1.0]])]});}
            var Q29;
            {var subQ0=sQuery(id+"F0.wireOp",EDGE,"E41.0");var subQ1=sQuery(id+"F0.wireOp",EDGE,"E26");var subQ2=makeQuery(id+"F0.imprint","INTERSECT",VERTEX,{"derivedFrom":[subQ1,subQ0]});Q29=makeQuery(id+"F0.imprint","IMPRINT",FACE,{"disambiguationData":[TD([[makeQuery(id+"F0.imprint","IMPRINT",EDGE,{"disambiguationData":[TD([[subQ2,1.0]])],"derivedFrom":subQ1}),-1.0]])]});}
            var Q30;
            {var subQ0=sQuery(id+"F0.wireOp",EDGE,"E42.0");var subQ1=sQuery(id+"F0.wireOp",EDGE,"E26");var subQ2=makeQuery(id+"F0.imprint","INTERSECT",VERTEX,{"derivedFrom":[subQ1,subQ0]});Q30=makeQuery(id+"F0.imprint","IMPRINT",FACE,{"disambiguationData":[TD([[makeQuery(id+"F0.imprint","IMPRINT",EDGE,{"disambiguationData":[TD([[subQ2,1.0]])],"derivedFrom":subQ1}),-1.0]])]});}
            var Q31;
            {var subQ0=sQuery(id+"F0.wireOp",EDGE,"E43.0");var subQ1=sQuery(id+"F0.wireOp",EDGE,"E26");var subQ2=makeQuery(id+"F0.imprint","INTERSECT",VERTEX,{"derivedFrom":[subQ1,subQ0]});Q31=makeQuery(id+"F0.imprint","IMPRINT",FACE,{"disambiguationData":[TD([[makeQuery(id+"F0.imprint","IMPRINT",EDGE,{"disambiguationData":[TD([[subQ2,1.0]])],"derivedFrom":subQ1}),-1.0]])]});}
            var Q32;
            {var subQ0=sQuery(id+"F0.wireOp",EDGE,"E39.0");var subQ1=sQuery(id+"F0.wireOp",EDGE,"E26");var subQ2=makeQuery(id+"F0.imprint","INTERSECT",VERTEX,{"derivedFrom":[subQ1,subQ0]});Q32=makeQuery(id+"F0.imprint","IMPRINT",FACE,{"disambiguationData":[TD([[makeQuery(id+"F0.imprint","IMPRINT",EDGE,{"disambiguationData":[TD([[subQ2,-1.0]])],"derivedFrom":subQ1}),-1.0]])]});}
            var Q33;
            {var subQ0=sQuery(id+"F0.wireOp",EDGE,"E39.0");var subQ1=sQuery(id+"F0.wireOp",EDGE,"E26");var subQ2=makeQuery(id+"F0.imprint","INTERSECT",VERTEX,{"derivedFrom":[subQ1,subQ0]});Q33=makeQuery(id+"F0.imprint","IMPRINT",FACE,{"disambiguationData":[TD([[makeQuery(id+"F0.imprint","IMPRINT",EDGE,{"disambiguationData":[TD([[subQ2,1.0]])],"derivedFrom":subQ1}),-1.0]])]});}
            var Q34;
            {var subQ0=sQuery(id+"F0.wireOp",EDGE,"E37.0");var subQ1=sQuery(id+"F0.wireOp",EDGE,"E26");var subQ2=makeQuery(id+"F0.imprint","INTERSECT",VERTEX,{"derivedFrom":[subQ1,subQ0]});Q34=makeQuery(id+"F0.imprint","IMPRINT",FACE,{"disambiguationData":[TD([[makeQuery(id+"F0.imprint","IMPRINT",EDGE,{"disambiguationData":[TD([[subQ2,-1.0]])],"derivedFrom":subQ1}),-1.0]])]});}
            var Q35;
            {var subQ0=sQuery(id+"F0.wireOp",EDGE,"E37.0");var subQ1=sQuery(id+"F0.wireOp",EDGE,"E26");var subQ2=makeQuery(id+"F0.imprint","INTERSECT",VERTEX,{"derivedFrom":[subQ1,subQ0]});Q35=makeQuery(id+"F0.imprint","IMPRINT",FACE,{"disambiguationData":[TD([[makeQuery(id+"F0.imprint","IMPRINT",EDGE,{"disambiguationData":[TD([[subQ2,1.0]])],"derivedFrom":subQ1}),-1.0]])]});}
            var Q36;
            {var subQ0=sQuery(id+"F0.wireOp",EDGE,"E35.0");var subQ1=sQuery(id+"F0.wireOp",EDGE,"E26");var subQ2=makeQuery(id+"F0.imprint","INTERSECT",VERTEX,{"derivedFrom":[subQ1,subQ0]});Q36=makeQuery(id+"F0.imprint","IMPRINT",FACE,{"disambiguationData":[TD([[makeQuery(id+"F0.imprint","IMPRINT",EDGE,{"disambiguationData":[TD([[subQ2,-1.0]])],"derivedFrom":subQ1}),-1.0]])]});}
            var Q37;
            {var subQ0=sQuery(id+"F0.wireOp",EDGE,"E35.0");var subQ1=sQuery(id+"F0.wireOp",EDGE,"E26");var subQ2=makeQuery(id+"F0.imprint","INTERSECT",VERTEX,{"derivedFrom":[subQ1,subQ0]});Q37=makeQuery(id+"F0.imprint","IMPRINT",FACE,{"disambiguationData":[TD([[makeQuery(id+"F0.imprint","IMPRINT",EDGE,{"disambiguationData":[TD([[subQ2,1.0]])],"derivedFrom":subQ1}),-1.0]])]});}
            var Q38;
            {var subQ0=sQuery(id+"F0.wireOp",EDGE,"E33.0");var subQ1=sQuery(id+"F0.wireOp",EDGE,"E26");var subQ2=makeQuery(id+"F0.imprint","INTERSECT",VERTEX,{"derivedFrom":[subQ1,subQ0]});Q38=makeQuery(id+"F0.imprint","IMPRINT",FACE,{"disambiguationData":[TD([[makeQuery(id+"F0.imprint","IMPRINT",EDGE,{"disambiguationData":[TD([[subQ2,-1.0]])],"derivedFrom":subQ1}),-1.0]])]});}
            var Q39;
            {var subQ0=sQuery(id+"F0.wireOp",EDGE,"E33.0");var subQ1=sQuery(id+"F0.wireOp",EDGE,"E26");var subQ2=makeQuery(id+"F0.imprint","INTERSECT",VERTEX,{"derivedFrom":[subQ1,subQ0]});Q39=makeQuery(id+"F0.imprint","IMPRINT",FACE,{"disambiguationData":[TD([[makeQuery(id+"F0.imprint","IMPRINT",EDGE,{"disambiguationData":[TD([[subQ2,1.0]])],"derivedFrom":subQ1}),-1.0]])]});}
            var Q40;
            {var subQ0=sQuery(id+"F0.wireOp",EDGE,"E31.0");var subQ1=sQuery(id+"F0.wireOp",EDGE,"E26");var subQ2=makeQuery(id+"F0.imprint","INTERSECT",VERTEX,{"derivedFrom":[subQ1,subQ0]});Q40=makeQuery(id+"F0.imprint","IMPRINT",FACE,{"disambiguationData":[TD([[makeQuery(id+"F0.imprint","IMPRINT",EDGE,{"disambiguationData":[TD([[subQ2,-1.0]])],"derivedFrom":subQ1}),-1.0]])]});}
            var Q41;
            {var subQ0=sQuery(id+"F0.wireOp",EDGE,"E31.0");var subQ1=sQuery(id+"F0.wireOp",EDGE,"E26");var subQ2=makeQuery(id+"F0.imprint","INTERSECT",VERTEX,{"derivedFrom":[subQ1,subQ0]});Q41=makeQuery(id+"F0.imprint","IMPRINT",FACE,{"disambiguationData":[TD([[makeQuery(id+"F0.imprint","IMPRINT",EDGE,{"disambiguationData":[TD([[subQ2,1.0]])],"derivedFrom":subQ1}),-1.0]])]});}
            var Q42;
            {var subQ0=sQuery(id+"F0.wireOp",EDGE,"E26");var subQ1=sQuery(id+"F0.wireOp",EDGE,"E20.top");var subQ2=makeQuery(id+"F0.imprint","INTERSECT",VERTEX,{"disambiguationData":[OD(0.0)],"derivedFrom":[subQ1,subQ0]});Q42=makeQuery(id+"F0.imprint","IMPRINT",FACE,{"disambiguationData":[TD([[makeQuery(id+"F0.imprint","IMPRINT",EDGE,{"disambiguationData":[TD([[subQ2,-1.0]])],"derivedFrom":subQ1}),1.0]])]});}
            var Q43;
            {var subQ10=sQuery(id+"F0.wireOp",EDGE,"E28");Q43=makeQuery(id+"F0.imprint","IMPRINT",FACE,{"disambiguationData":[TD([[makeQuery(id+"F0.imprint","IMPRINT",EDGE,{"derivedFrom":subQ10}),1.0]])]});}
            var Q44;
            {var subQ0=sQuery(id+"F0.wireOp",EDGE,"E34.MirrorCS");var subQ3=sQuery(id+"F0.wireOp",EDGE,"E27");var subQ4=makeQuery(id+"F0.imprint","INTERSECT",VERTEX,{"derivedFrom":[subQ3,subQ0]});Q44=makeQuery(id+"F0.imprint","IMPRINT",FACE,{"disambiguationData":[TD([[makeQuery(id+"F0.imprint","IMPRINT",EDGE,{"disambiguationData":[TD([[subQ4,-1.0]])],"derivedFrom":subQ3}),-1.0]])]});}
            var Q45;
            {var subQ0=sQuery(id+"F0.wireOp",EDGE,"E38.0");var subQ3=sQuery(id+"F0.wireOp",EDGE,"E27");var subQ4=makeQuery(id+"F0.imprint","INTERSECT",VERTEX,{"derivedFrom":[subQ3,subQ0]});Q45=makeQuery(id+"F0.imprint","IMPRINT",FACE,{"disambiguationData":[TD([[makeQuery(id+"F0.imprint","IMPRINT",EDGE,{"disambiguationData":[TD([[subQ4,-1.0]])],"derivedFrom":subQ3}),-1.0]])]});}
            var Q46;
            {var subQ0=sQuery(id+"F0.wireOp",EDGE,"E33.0");var subQ1=sQuery(id+"F0.wireOp",EDGE,"E24");var subQ2=makeQuery(id+"F0.imprint","INTERSECT",VERTEX,{"derivedFrom":[subQ1,subQ0]});Q46=makeQuery(id+"F0.imprint","IMPRINT",FACE,{"disambiguationData":[TD([[makeQuery(id+"F0.imprint","IMPRINT",EDGE,{"disambiguationData":[TD([[subQ2,-1.0]])],"derivedFrom":subQ1}),-1.0]])]});}
            extrude(context, id + "F2", {"entities" : qUnion([Q0, Q1, Q2, Q3, Q4, Q5, Q6, Q7, Q8, Q9, Q10, Q11, Q12, Q13, Q14, Q15, Q16, Q17, Q18, Q19, Q20, Q21, Q22, Q23, Q24, Q25, Q26, Q27, Q28, Q29, Q30, Q31, Q32, Q33, Q34, Q35, Q36, Q37, Q38, Q39, Q40, Q41, Q42, Q43, Q44, Q45, Q46]), "operationType" : NewBodyOperationType.ADD, "depth" : 1.5 * mm, "offsetDistance" : 25 * mm});
        }
        {
            var Q0;
            {var subQ26=sQuery(id+"F0.wireOp",EDGE,"E13.top");Q0=makeQuery(id+"F0.imprint","IMPRINT",FACE,{"disambiguationData":[TD([[makeQuery(id+"F0.imprint","IMPRINT",EDGE,{"derivedFrom":subQ26}),-1.0]])]});}
            extrude(context, id + "F3", {"entities" : qUnion([Q0]), "operationType" : NewBodyOperationType.ADD, "depth" : 2 * mm, "offsetDistance" : 25 * mm});
        }
        {
            var Q0;
            Q0=makeQuery(id+"F3.opExtrude","CAP_EDGE",EDGE,{"disambiguationData":[OSD([sQuery(id+"F0.wireOp",EDGE,"E18.4.5.4")])],"isStart":false});
            var Q1;
            Q1=makeQuery(id+"F3.opExtrude","CAP_EDGE",EDGE,{"disambiguationData":[OSD([sQuery(id+"F0.wireOp",EDGE,"E18.4.5.3")])],"isStart":false});
            var Q2;
            Q2=makeQuery(id+"F3.opExtrude","CAP_EDGE",EDGE,{"disambiguationData":[OSD([sQuery(id+"F0.wireOp",EDGE,"E18.3.5.4")])],"isStart":false});
            var Q3;
            Q3=makeQuery(id+"F3.opExtrude","CAP_EDGE",EDGE,{"disambiguationData":[OSD([sQuery(id+"F0.wireOp",EDGE,"E18.3.5.3")])],"isStart":false});
            var Q4;
            Q4=makeQuery(id+"F3.opExtrude","CAP_EDGE",EDGE,{"disambiguationData":[OSD([sQuery(id+"F0.wireOp",EDGE,"E18.2.5.4")])],"isStart":false});
            var Q5;
            Q5=makeQuery(id+"F3.opExtrude","CAP_EDGE",EDGE,{"disambiguationData":[OSD([sQuery(id+"F0.wireOp",EDGE,"E18.2.5.3")])],"isStart":false});
            var Q6;
            Q6=makeQuery(id+"F3.opExtrude","CAP_EDGE",EDGE,{"disambiguationData":[OSD([sQuery(id+"F0.wireOp",EDGE,"E18.1.5.4")])],"isStart":false});
            var Q7;
            Q7=makeQuery(id+"F3.opExtrude","CAP_EDGE",EDGE,{"disambiguationData":[OSD([sQuery(id+"F0.wireOp",EDGE,"E18.1.5.3")])],"isStart":false});
            var Q8;
            Q8=makeQuery(id+"F3.opExtrude","CAP_EDGE",EDGE,{"disambiguationData":[OSD([sQuery(id+"F0.wireOp",EDGE,"E18.1.4.1")])],"isStart":false});
            var Q9;
            Q9=makeQuery(id+"F3.opExtrude","CAP_EDGE",EDGE,{"disambiguationData":[OSD([sQuery(id+"F0.wireOp",EDGE,"E18.1.4.2")])],"isStart":false});
            var Q10;
            Q10=makeQuery(id+"F3.opExtrude","CAP_EDGE",EDGE,{"disambiguationData":[OSD([sQuery(id+"F0.wireOp",EDGE,"E18.1.4.3")])],"isStart":false});
            var Q11;
            Q11=makeQuery(id+"F3.opExtrude","CAP_EDGE",EDGE,{"disambiguationData":[OSD([sQuery(id+"F0.wireOp",EDGE,"E18.1.4.4")])],"isStart":false});
            var Q12;
            Q12=makeQuery(id+"F3.opExtrude","CAP_EDGE",EDGE,{"disambiguationData":[OSD([sQuery(id+"F0.wireOp",EDGE,"E18.2.4.2")])],"isStart":false});
            var Q13;
            Q13=makeQuery(id+"F3.opExtrude","CAP_EDGE",EDGE,{"disambiguationData":[OSD([sQuery(id+"F0.wireOp",EDGE,"E18.2.4.1")])],"isStart":false});
            var Q14;
            Q14=makeQuery(id+"F3.opExtrude","CAP_EDGE",EDGE,{"disambiguationData":[OSD([sQuery(id+"F0.wireOp",EDGE,"E18.3.4.2")])],"isStart":false});
            var Q15;
            Q15=makeQuery(id+"F3.opExtrude","CAP_EDGE",EDGE,{"disambiguationData":[OSD([sQuery(id+"F0.wireOp",EDGE,"E18.3.4.1")])],"isStart":false});
            var Q16;
            Q16=makeQuery(id+"F3.opExtrude","CAP_EDGE",EDGE,{"disambiguationData":[OSD([sQuery(id+"F0.wireOp",EDGE,"E18.4.4.1")])],"isStart":false});
            var Q17;
            Q17=makeQuery(id+"F3.opExtrude","CAP_EDGE",EDGE,{"disambiguationData":[OSD([sQuery(id+"F0.wireOp",EDGE,"E18.4.4.2")])],"isStart":false});
            var Q18;
            Q18=makeQuery(id+"F3.opExtrude","CAP_EDGE",EDGE,{"disambiguationData":[OSD([sQuery(id+"F0.wireOp",EDGE,"E18.5.4.1")])],"isStart":false});
            var Q19;
            Q19=makeQuery(id+"F3.opExtrude","CAP_EDGE",EDGE,{"disambiguationData":[OSD([sQuery(id+"F0.wireOp",EDGE,"E18.5.4.2")])],"isStart":false});
            var Q20;
            Q20=makeQuery(id+"F3.opExtrude","CAP_EDGE",EDGE,{"disambiguationData":[OSD([sQuery(id+"F0.wireOp",EDGE,"E18.4.4.4")])],"isStart":false});
            var Q21;
            Q21=makeQuery(id+"F3.opExtrude","CAP_EDGE",EDGE,{"disambiguationData":[OSD([sQuery(id+"F0.wireOp",EDGE,"E18.4.4.3")])],"isStart":false});
            var Q22;
            Q22=makeQuery(id+"F3.opExtrude","CAP_EDGE",EDGE,{"disambiguationData":[OSD([sQuery(id+"F0.wireOp",EDGE,"E18.4.3.4")])],"isStart":false});
            var Q23;
            Q23=makeQuery(id+"F3.opExtrude","CAP_EDGE",EDGE,{"disambiguationData":[OSD([sQuery(id+"F0.wireOp",EDGE,"E18.4.3.3")])],"isStart":false});
            var Q24;
            Q24=makeQuery(id+"F3.opExtrude","CAP_EDGE",EDGE,{"disambiguationData":[OSD([sQuery(id+"F0.wireOp",EDGE,"E18.3.3.4")])],"isStart":false});
            var Q25;
            Q25=makeQuery(id+"F3.opExtrude","CAP_EDGE",EDGE,{"disambiguationData":[OSD([sQuery(id+"F0.wireOp",EDGE,"E18.3.4.4")])],"isStart":false});
            var Q26;
            Q26=makeQuery(id+"F3.opExtrude","CAP_EDGE",EDGE,{"disambiguationData":[OSD([sQuery(id+"F0.wireOp",EDGE,"E18.3.4.3")])],"isStart":false});
            var Q27;
            Q27=makeQuery(id+"F3.opExtrude","CAP_EDGE",EDGE,{"disambiguationData":[OSD([sQuery(id+"F0.wireOp",EDGE,"E18.2.4.4")])],"isStart":false});
            var Q28;
            Q28=makeQuery(id+"F3.opExtrude","CAP_EDGE",EDGE,{"disambiguationData":[OSD([sQuery(id+"F0.wireOp",EDGE,"E18.2.4.3")])],"isStart":false});
            var Q29;
            Q29=makeQuery(id+"F3.opExtrude","CAP_EDGE",EDGE,{"disambiguationData":[OSD([sQuery(id+"F0.wireOp",EDGE,"E18.2.3.4")])],"isStart":false});
            var Q30;
            Q30=makeQuery(id+"F3.opExtrude","CAP_EDGE",EDGE,{"disambiguationData":[OSD([sQuery(id+"F0.wireOp",EDGE,"E18.2.3.3")])],"isStart":false});
            var Q31;
            Q31=makeQuery(id+"F3.opExtrude","CAP_EDGE",EDGE,{"disambiguationData":[OSD([sQuery(id+"F0.wireOp",EDGE,"E18.1.3.4")])],"isStart":false});
            var Q32;
            Q32=makeQuery(id+"F3.opExtrude","CAP_EDGE",EDGE,{"disambiguationData":[OSD([sQuery(id+"F0.wireOp",EDGE,"E18.1.3.3")])],"isStart":false});
            var Q33;
            Q33=makeQuery(id+"F3.opExtrude","CAP_EDGE",EDGE,{"disambiguationData":[OSD([sQuery(id+"F0.wireOp",EDGE,"E18.0.3.4")])],"isStart":false});
            var Q34;
            Q34=makeQuery(id+"F3.opExtrude","CAP_EDGE",EDGE,{"disambiguationData":[OSD([sQuery(id+"F0.wireOp",EDGE,"E18.0.3.3")])],"isStart":false});
            var Q35;
            Q35=makeQuery(id+"F3.opExtrude","CAP_EDGE",EDGE,{"disambiguationData":[OSD([sQuery(id+"F0.wireOp",EDGE,"E18.0.4.4")])],"isStart":false});
            var Q36;
            Q36=makeQuery(id+"F3.opExtrude","CAP_EDGE",EDGE,{"disambiguationData":[OSD([sQuery(id+"F0.wireOp",EDGE,"E18.0.4.3")])],"isStart":false});
            var Q37;
            Q37=makeQuery(id+"F3.opExtrude","CAP_EDGE",EDGE,{"disambiguationData":[OSD([sQuery(id+"F0.wireOp",EDGE,"E18.0.5.4")])],"isStart":false});
            var Q38;
            Q38=makeQuery(id+"F3.opExtrude","CAP_EDGE",EDGE,{"disambiguationData":[OSD([sQuery(id+"F0.wireOp",EDGE,"E18.0.5.3")])],"isStart":false});
            var Q39;
            Q39=makeQuery(id+"F3.opExtrude","CAP_EDGE",EDGE,{"disambiguationData":[OSD([sQuery(id+"F0.wireOp",EDGE,"E18.0.4.1")])],"isStart":false});
            var Q40;
            Q40=makeQuery(id+"F3.opExtrude","CAP_EDGE",EDGE,{"disambiguationData":[OSD([sQuery(id+"F0.wireOp",EDGE,"E18.0.4.2")])],"isStart":false});
            var Q41;
            Q41=makeQuery(id+"F3.opExtrude","CAP_EDGE",EDGE,{"disambiguationData":[OSD([sQuery(id+"F0.wireOp",EDGE,"E18.0.3.2")])],"isStart":false});
            var Q42;
            Q42=makeQuery(id+"F3.opExtrude","CAP_EDGE",EDGE,{"disambiguationData":[OSD([sQuery(id+"F0.wireOp",EDGE,"E18.0.3.1")])],"isStart":false});
            var Q43;
            Q43=makeQuery(id+"F3.opExtrude","CAP_EDGE",EDGE,{"disambiguationData":[OSD([sQuery(id+"F0.wireOp",EDGE,"E18.1.3.2")])],"isStart":false});
            var Q44;
            Q44=makeQuery(id+"F3.opExtrude","CAP_EDGE",EDGE,{"disambiguationData":[OSD([sQuery(id+"F0.wireOp",EDGE,"E18.1.3.1")])],"isStart":false});
            var Q45;
            Q45=makeQuery(id+"F3.opExtrude","CAP_EDGE",EDGE,{"disambiguationData":[OSD([sQuery(id+"F0.wireOp",EDGE,"E18.2.3.2")])],"isStart":false});
            var Q46;
            Q46=makeQuery(id+"F3.opExtrude","CAP_EDGE",EDGE,{"disambiguationData":[OSD([sQuery(id+"F0.wireOp",EDGE,"E18.2.3.1")])],"isStart":false});
            var Q47;
            Q47=makeQuery(id+"F3.opExtrude","CAP_EDGE",EDGE,{"disambiguationData":[OSD([sQuery(id+"F0.wireOp",EDGE,"E18.3.3.2")])],"isStart":false});
            var Q48;
            Q48=makeQuery(id+"F3.opExtrude","CAP_EDGE",EDGE,{"disambiguationData":[OSD([sQuery(id+"F0.wireOp",EDGE,"E18.3.3.1")])],"isStart":false});
            var Q49;
            Q49=makeQuery(id+"F3.opExtrude","CAP_EDGE",EDGE,{"disambiguationData":[OSD([sQuery(id+"F0.wireOp",EDGE,"E18.4.3.2")])],"isStart":false});
            var Q50;
            Q50=makeQuery(id+"F3.opExtrude","CAP_EDGE",EDGE,{"disambiguationData":[OSD([sQuery(id+"F0.wireOp",EDGE,"E18.4.3.1")])],"isStart":false});
            var Q51;
            Q51=makeQuery(id+"F3.opExtrude","CAP_EDGE",EDGE,{"disambiguationData":[OSD([sQuery(id+"F0.wireOp",EDGE,"E18.3.3.3")])],"isStart":false});
            var Q52;
            Q52=makeQuery(id+"F3.opExtrude","CAP_EDGE",EDGE,{"disambiguationData":[OSD([sQuery(id+"F0.wireOp",EDGE,"E18.5.3.1")])],"isStart":false});
            var Q53;
            Q53=makeQuery(id+"F3.opExtrude","CAP_EDGE",EDGE,{"disambiguationData":[OSD([sQuery(id+"F0.wireOp",EDGE,"E18.5.3.2")])],"isStart":false});
            var Q54;
            Q54=makeQuery(id+"F3.opExtrude","CAP_EDGE",EDGE,{"disambiguationData":[OSD([sQuery(id+"F0.wireOp",EDGE,"E18.5.2.1")])],"isStart":false});
            var Q55;
            Q55=makeQuery(id+"F3.opExtrude","CAP_EDGE",EDGE,{"disambiguationData":[OSD([sQuery(id+"F0.wireOp",EDGE,"E18.5.2.2")])],"isStart":false});
            var Q56;
            Q56=makeQuery(id+"F3.opExtrude","CAP_EDGE",EDGE,{"disambiguationData":[OSD([sQuery(id+"F0.wireOp",EDGE,"E18.4.2.4")])],"isStart":false});
            var Q57;
            Q57=makeQuery(id+"F3.opExtrude","CAP_EDGE",EDGE,{"disambiguationData":[OSD([sQuery(id+"F0.wireOp",EDGE,"E18.4.2.3")])],"isStart":false});
            var Q58;
            Q58=makeQuery(id+"F3.opExtrude","CAP_EDGE",EDGE,{"disambiguationData":[OSD([sQuery(id+"F0.wireOp",EDGE,"E18.4.2.1")])],"isStart":false});
            var Q59;
            Q59=makeQuery(id+"F3.opExtrude","CAP_EDGE",EDGE,{"disambiguationData":[OSD([sQuery(id+"F0.wireOp",EDGE,"E18.4.2.2")])],"isStart":false});
            var Q60;
            Q60=makeQuery(id+"F3.opExtrude","CAP_EDGE",EDGE,{"disambiguationData":[OSD([sQuery(id+"F0.wireOp",EDGE,"E18.3.2.1")])],"isStart":false});
            var Q61;
            Q61=makeQuery(id+"F3.opExtrude","CAP_EDGE",EDGE,{"disambiguationData":[OSD([sQuery(id+"F0.wireOp",EDGE,"E18.3.2.2")])],"isStart":false});
            var Q62;
            Q62=makeQuery(id+"F3.opExtrude","CAP_EDGE",EDGE,{"disambiguationData":[OSD([sQuery(id+"F0.wireOp",EDGE,"E18.2.2.1")])],"isStart":false});
            var Q63;
            Q63=makeQuery(id+"F3.opExtrude","CAP_EDGE",EDGE,{"disambiguationData":[OSD([sQuery(id+"F0.wireOp",EDGE,"E18.2.2.2")])],"isStart":false});
            var Q64;
            Q64=makeQuery(id+"F3.opExtrude","CAP_EDGE",EDGE,{"disambiguationData":[OSD([sQuery(id+"F0.wireOp",EDGE,"E18.1.2.1")])],"isStart":false});
            var Q65;
            Q65=makeQuery(id+"F3.opExtrude","CAP_EDGE",EDGE,{"disambiguationData":[OSD([sQuery(id+"F0.wireOp",EDGE,"E18.1.2.2")])],"isStart":false});
            var Q66;
            Q66=makeQuery(id+"F3.opExtrude","CAP_EDGE",EDGE,{"disambiguationData":[OSD([sQuery(id+"F0.wireOp",EDGE,"E18.0.2.1")])],"isStart":false});
            var Q67;
            Q67=makeQuery(id+"F3.opExtrude","CAP_EDGE",EDGE,{"disambiguationData":[OSD([sQuery(id+"F0.wireOp",EDGE,"E18.0.2.2")])],"isStart":false});
            var Q68;
            Q68=makeQuery(id+"F3.opExtrude","CAP_EDGE",EDGE,{"disambiguationData":[OSD([sQuery(id+"F0.wireOp",EDGE,"E18.0.2.3")])],"isStart":false});
            var Q69;
            Q69=makeQuery(id+"F3.opExtrude","CAP_EDGE",EDGE,{"disambiguationData":[OSD([sQuery(id+"F0.wireOp",EDGE,"E18.0.2.4")])],"isStart":false});
            var Q70;
            Q70=makeQuery(id+"F3.opExtrude","CAP_EDGE",EDGE,{"disambiguationData":[OSD([sQuery(id+"F0.wireOp",EDGE,"E18.0.1.1")])],"isStart":false});
            var Q71;
            Q71=makeQuery(id+"F3.opExtrude","CAP_EDGE",EDGE,{"disambiguationData":[OSD([sQuery(id+"F0.wireOp",EDGE,"E18.0.1.2")])],"isStart":false});
            var Q72;
            Q72=makeQuery(id+"F3.opExtrude","CAP_EDGE",EDGE,{"disambiguationData":[OSD([sQuery(id+"F0.wireOp",EDGE,"E15.top")])],"isStart":false});
            var Q73;
            Q73=makeQuery(id+"F3.opExtrude","CAP_EDGE",EDGE,{"disambiguationData":[OSD([sQuery(id+"F0.wireOp",EDGE,"E13.top")])],"isStart":false});
            var Q74;
            Q74=makeQuery(id+"F3.opExtrude","CAP_EDGE",EDGE,{"disambiguationData":[OSD([sQuery(id+"F0.wireOp",EDGE,"E18.0.1.3")])],"isStart":false});
            var Q75;
            Q75=makeQuery(id+"F3.opExtrude","CAP_EDGE",EDGE,{"disambiguationData":[OSD([sQuery(id+"F0.wireOp",EDGE,"E18.0.1.4")])],"isStart":false});
            var Q76;
            Q76=makeQuery(id+"F3.opExtrude","CAP_EDGE",EDGE,{"disambiguationData":[OSD([sQuery(id+"F0.wireOp",EDGE,"E13.right")])],"isStart":false});
            var Q77;
            Q77=makeQuery(id+"F3.opExtrude","CAP_EDGE",EDGE,{"disambiguationData":[OSD([sQuery(id+"F0.wireOp",EDGE,"E14.right")])],"isStart":false});
            var Q78;
            Q78=makeQuery(id+"F3.opExtrude","CAP_EDGE",EDGE,{"disambiguationData":[OSD([sQuery(id+"F0.wireOp",EDGE,"E18.1.0.2")])],"isStart":false});
            var Q79;
            Q79=makeQuery(id+"F3.opExtrude","CAP_EDGE",EDGE,{"disambiguationData":[OSD([sQuery(id+"F0.wireOp",EDGE,"E18.1.0.1")])],"isStart":false});
            var Q80;
            Q80=makeQuery(id+"F3.opExtrude","CAP_EDGE",EDGE,{"disambiguationData":[OSD([sQuery(id+"F0.wireOp",EDGE,"E18.1.1.2")])],"isStart":false});
            var Q81;
            Q81=makeQuery(id+"F3.opExtrude","CAP_EDGE",EDGE,{"disambiguationData":[OSD([sQuery(id+"F0.wireOp",EDGE,"E18.1.1.1")])],"isStart":false});
            var Q82;
            Q82=makeQuery(id+"F3.opExtrude","CAP_EDGE",EDGE,{"disambiguationData":[OSD([sQuery(id+"F0.wireOp",EDGE,"E18.1.0.3")])],"isStart":false});
            var Q83;
            Q83=makeQuery(id+"F3.opExtrude","CAP_EDGE",EDGE,{"disambiguationData":[OSD([sQuery(id+"F0.wireOp",EDGE,"E18.1.0.4")])],"isStart":false});
            var Q84;
            Q84=makeQuery(id+"F3.opExtrude","CAP_EDGE",EDGE,{"disambiguationData":[OSD([sQuery(id+"F0.wireOp",EDGE,"E18.1.1.4")])],"isStart":false});
            var Q85;
            Q85=makeQuery(id+"F3.opExtrude","CAP_EDGE",EDGE,{"disambiguationData":[OSD([sQuery(id+"F0.wireOp",EDGE,"E18.1.1.3")])],"isStart":false});
            var Q86;
            Q86=makeQuery(id+"F3.opExtrude","CAP_EDGE",EDGE,{"disambiguationData":[OSD([sQuery(id+"F0.wireOp",EDGE,"E18.1.2.4")])],"isStart":false});
            var Q87;
            Q87=makeQuery(id+"F3.opExtrude","CAP_EDGE",EDGE,{"disambiguationData":[OSD([sQuery(id+"F0.wireOp",EDGE,"E18.1.2.3")])],"isStart":false});
            var Q88;
            Q88=makeQuery(id+"F3.opExtrude","CAP_EDGE",EDGE,{"disambiguationData":[OSD([sQuery(id+"F0.wireOp",EDGE,"E18.2.1.1")])],"isStart":false});
            var Q89;
            Q89=makeQuery(id+"F3.opExtrude","CAP_EDGE",EDGE,{"disambiguationData":[OSD([sQuery(id+"F0.wireOp",EDGE,"E18.2.1.2")])],"isStart":false});
            var Q90;
            Q90=makeQuery(id+"F3.opExtrude","CAP_EDGE",EDGE,{"disambiguationData":[OSD([sQuery(id+"F0.wireOp",EDGE,"E18.2.0.1")])],"isStart":false});
            var Q91;
            Q91=makeQuery(id+"F3.opExtrude","CAP_EDGE",EDGE,{"disambiguationData":[OSD([sQuery(id+"F0.wireOp",EDGE,"E18.2.0.2")])],"isStart":false});
            var Q92;
            Q92=makeQuery(id+"F3.opExtrude","CAP_EDGE",EDGE,{"disambiguationData":[OSD([sQuery(id+"F0.wireOp",EDGE,"E18.2.2.3")])],"isStart":false});
            var Q93;
            Q93=makeQuery(id+"F3.opExtrude","CAP_EDGE",EDGE,{"disambiguationData":[OSD([sQuery(id+"F0.wireOp",EDGE,"E18.2.2.4")])],"isStart":false});
            var Q94;
            Q94=makeQuery(id+"F3.opExtrude","CAP_EDGE",EDGE,{"disambiguationData":[OSD([sQuery(id+"F0.wireOp",EDGE,"E18.2.1.4")])],"isStart":false});
            var Q95;
            Q95=makeQuery(id+"F3.opExtrude","CAP_EDGE",EDGE,{"disambiguationData":[OSD([sQuery(id+"F0.wireOp",EDGE,"E18.2.1.3")])],"isStart":false});
            var Q96;
            Q96=makeQuery(id+"F3.opExtrude","CAP_EDGE",EDGE,{"disambiguationData":[OSD([sQuery(id+"F0.wireOp",EDGE,"E18.2.0.4")])],"isStart":false});
            var Q97;
            Q97=makeQuery(id+"F3.opExtrude","CAP_EDGE",EDGE,{"disambiguationData":[OSD([sQuery(id+"F0.wireOp",EDGE,"E18.2.0.3")])],"isStart":false});
            var Q98;
            Q98=makeQuery(id+"F3.opExtrude","CAP_EDGE",EDGE,{"disambiguationData":[OSD([sQuery(id+"F0.wireOp",EDGE,"E18.3.0.2")])],"isStart":false});
            var Q99;
            Q99=makeQuery(id+"F3.opExtrude","CAP_EDGE",EDGE,{"disambiguationData":[OSD([sQuery(id+"F0.wireOp",EDGE,"E18.3.0.1")])],"isStart":false});
            var Q100;
            Q100=makeQuery(id+"F3.opExtrude","CAP_EDGE",EDGE,{"disambiguationData":[OSD([sQuery(id+"F0.wireOp",EDGE,"E18.3.1.2")])],"isStart":false});
            var Q101;
            Q101=makeQuery(id+"F3.opExtrude","CAP_EDGE",EDGE,{"disambiguationData":[OSD([sQuery(id+"F0.wireOp",EDGE,"E18.3.1.1")])],"isStart":false});
            var Q102;
            Q102=makeQuery(id+"F3.opExtrude","CAP_EDGE",EDGE,{"disambiguationData":[OSD([sQuery(id+"F0.wireOp",EDGE,"E18.3.0.3")])],"isStart":false});
            var Q103;
            Q103=makeQuery(id+"F3.opExtrude","CAP_EDGE",EDGE,{"disambiguationData":[OSD([sQuery(id+"F0.wireOp",EDGE,"E18.3.0.4")])],"isStart":false});
            var Q104;
            Q104=makeQuery(id+"F3.opExtrude","CAP_EDGE",EDGE,{"disambiguationData":[OSD([sQuery(id+"F0.wireOp",EDGE,"E18.3.1.4")])],"isStart":false});
            var Q105;
            Q105=makeQuery(id+"F3.opExtrude","CAP_EDGE",EDGE,{"disambiguationData":[OSD([sQuery(id+"F0.wireOp",EDGE,"E18.3.1.3")])],"isStart":false});
            var Q106;
            Q106=makeQuery(id+"F3.opExtrude","CAP_EDGE",EDGE,{"disambiguationData":[OSD([sQuery(id+"F0.wireOp",EDGE,"E18.3.2.3")])],"isStart":false});
            var Q107;
            Q107=makeQuery(id+"F3.opExtrude","CAP_EDGE",EDGE,{"disambiguationData":[OSD([sQuery(id+"F0.wireOp",EDGE,"E18.3.2.4")])],"isStart":false});
            var Q108;
            Q108=makeQuery(id+"F3.opExtrude","CAP_EDGE",EDGE,{"disambiguationData":[OSD([sQuery(id+"F0.wireOp",EDGE,"E18.4.1.2")])],"isStart":false});
            var Q109;
            Q109=makeQuery(id+"F3.opExtrude","CAP_EDGE",EDGE,{"disambiguationData":[OSD([sQuery(id+"F0.wireOp",EDGE,"E18.4.1.1")])],"isStart":false});
            var Q110;
            Q110=makeQuery(id+"F3.opExtrude","CAP_EDGE",EDGE,{"disambiguationData":[OSD([sQuery(id+"F0.wireOp",EDGE,"E18.4.1.4")])],"isStart":false});
            var Q111;
            Q111=makeQuery(id+"F3.opExtrude","CAP_EDGE",EDGE,{"disambiguationData":[OSD([sQuery(id+"F0.wireOp",EDGE,"E18.4.1.3")])],"isStart":false});
            var Q112;
            Q112=makeQuery(id+"F3.opExtrude","CAP_EDGE",EDGE,{"disambiguationData":[OSD([sQuery(id+"F0.wireOp",EDGE,"E18.5.1.2")])],"isStart":false});
            var Q113;
            Q113=makeQuery(id+"F3.opExtrude","CAP_EDGE",EDGE,{"disambiguationData":[OSD([sQuery(id+"F0.wireOp",EDGE,"E18.5.1.1")])],"isStart":false});
            var Q114;
            Q114=makeQuery(id+"F3.opExtrude","CAP_EDGE",EDGE,{"disambiguationData":[OSD([sQuery(id+"F0.wireOp",EDGE,"E18.5.0.1")])],"isStart":false});
            var Q115;
            Q115=makeQuery(id+"F3.opExtrude","CAP_EDGE",EDGE,{"disambiguationData":[OSD([sQuery(id+"F0.wireOp",EDGE,"E18.5.0.2")])],"isStart":false});
            var Q116;
            Q116=makeQuery(id+"F3.opExtrude","CAP_EDGE",EDGE,{"disambiguationData":[OSD([sQuery(id+"F0.wireOp",EDGE,"E18.4.0.4")])],"isStart":false});
            var Q117;
            Q117=makeQuery(id+"F3.opExtrude","CAP_EDGE",EDGE,{"disambiguationData":[OSD([sQuery(id+"F0.wireOp",EDGE,"E18.4.0.3")])],"isStart":false});
            var Q118;
            Q118=makeQuery(id+"F3.opExtrude","CAP_EDGE",EDGE,{"disambiguationData":[OSD([sQuery(id+"F0.wireOp",EDGE,"E18.4.0.1")])],"isStart":false});
            var Q119;
            Q119=makeQuery(id+"F3.opExtrude","CAP_EDGE",EDGE,{"disambiguationData":[OSD([sQuery(id+"F0.wireOp",EDGE,"E18.4.0.2")])],"isStart":false});
            fillet(context, id + "F4", {"entities" : qUnion([Q0, Q1, Q2, Q3, Q4, Q5, Q6, Q7, Q8, Q9, Q10, Q11, Q12, Q13, Q14, Q15, Q16, Q17, Q18, Q19, Q20, Q21, Q22, Q23, Q24, Q25, Q26, Q27, Q28, Q29, Q30, Q31, Q32, Q33, Q34, Q35, Q36, Q37, Q38, Q39, Q40, Q41, Q42, Q43, Q44, Q45, Q46, Q47, Q48, Q49, Q50, Q51, Q52, Q53, Q54, Q55, Q56, Q57, Q58, Q59, Q60, Q61, Q62, Q63, Q64, Q65, Q66, Q67, Q68, Q69, Q70, Q71, Q72, Q73, Q74, Q75, Q76, Q77, Q78, Q79, Q80, Q81, Q82, Q83, Q84, Q85, Q86, Q87, Q88, Q89, Q90, Q91, Q92, Q93, Q94, Q95, Q96, Q97, Q98, Q99, Q100, Q101, Q102, Q103, Q104, Q105, Q106, Q107, Q108, Q109, Q110, Q111, Q112, Q113, Q114, Q115, Q116, Q117, Q118, Q119]), "radius" : 0.5 * mm, "tangentPropagation" : true, "allowEdgeOverflow" : false});
        }
        {
            var Q0;
            {var subQ0=sQuery(id+"F0.wireOp",EDGE,"E25");Q0=makeQuery(id+"F2.opExtrude","CAP_EDGE",EDGE,{"disambiguationData":[OSD([subQ0]),TDD([makeQuery(id+"F0.imprint","IMPRINT",EDGE,{"disambiguationData":[TD([[makeQuery(id+"F0.imprint","INTERSECT",VERTEX,{"disambiguationData":[OD(0.0)],"derivedFrom":[sQuery(id+"F0.wireOp",EDGE,"E20.top"),subQ0]}),-1.0]])],"derivedFrom":subQ0})])],"isStart":false});}
            var Q1;
            {var subQ0=sQuery(id+"F0.wireOp",EDGE,"E24");Q1=makeQuery(id+"F2.opExtrude","CAP_EDGE",EDGE,{"disambiguationData":[OSD([subQ0]),TDD([makeQuery(id+"F0.imprint","IMPRINT",EDGE,{"disambiguationData":[TD([[makeQuery(id+"F0.imprint","INTERSECT",VERTEX,{"disambiguationData":[OD(0.0)],"derivedFrom":[sQuery(id+"F0.wireOp",EDGE,"E20.top"),subQ0]}),-1.0]])],"derivedFrom":subQ0})])],"isStart":false});}
            var Q2;
            {var subQ0=sQuery(id+"F0.wireOp",EDGE,"E32.MirrorCS");Q2=makeQuery(id+"F2.opExtrude","CAP_EDGE",EDGE,{"disambiguationData":[OSD([subQ0]),TDD([makeQuery(id+"F0.imprint","IMPRINT",EDGE,{"disambiguationData":[TD([[makeQuery(id+"F0.imprint","INTERSECT",VERTEX,{"derivedFrom":[sQuery(id+"F0.wireOp",EDGE,"E24"),subQ0]}),-1.0]])],"derivedFrom":subQ0})])],"isStart":false});}
            var Q3;
            {var subQ0=sQuery(id+"F0.wireOp",EDGE,"E31.0");Q3=makeQuery(id+"F2.opExtrude","CAP_EDGE",EDGE,{"disambiguationData":[OSD([subQ0]),TDD([makeQuery(id+"F0.imprint","IMPRINT",EDGE,{"disambiguationData":[TD([[makeQuery(id+"F0.imprint","INTERSECT",VERTEX,{"derivedFrom":[sQuery(id+"F0.wireOp",EDGE,"E26"),subQ0]}),-1.0]])],"derivedFrom":subQ0})])],"isStart":false});}
            var Q4;
            {var subQ0=sQuery(id+"F0.wireOp",EDGE,"E32.MirrorCS");Q4=makeQuery(id+"F2.opExtrude","CAP_EDGE",EDGE,{"disambiguationData":[OSD([subQ0]),TDD([makeQuery(id+"F0.imprint","IMPRINT",EDGE,{"disambiguationData":[TD([[makeQuery(id+"F0.imprint","INTERSECT",VERTEX,{"derivedFrom":[sQuery(id+"F0.wireOp",EDGE,"E26"),subQ0]}),-1.0]])],"derivedFrom":subQ0})])],"isStart":false});}
            var Q5;
            {var subQ0=sQuery(id+"F0.wireOp",EDGE,"E26");Q5=makeQuery(id+"F2.opExtrude","CAP_EDGE",EDGE,{"disambiguationData":[OSD([subQ0]),TDD([makeQuery(id+"F0.imprint","IMPRINT",EDGE,{"disambiguationData":[TD([[makeQuery(id+"F0.imprint","INTERSECT",VERTEX,{"disambiguationData":[OD(0.0)],"derivedFrom":[sQuery(id+"F0.wireOp",EDGE,"E20.top"),subQ0]}),-1.0]])],"derivedFrom":subQ0})])],"isStart":false});}
            var Q6;
            {var subQ0=sQuery(id+"F0.wireOp",EDGE,"E27");Q6=makeQuery(id+"F2.opExtrude","CAP_EDGE",EDGE,{"disambiguationData":[OSD([subQ0]),TDD([makeQuery(id+"F0.imprint","IMPRINT",EDGE,{"disambiguationData":[TD([[makeQuery(id+"F0.imprint","INTERSECT",VERTEX,{"derivedFrom":[subQ0,sQuery(id+"F0.wireOp",EDGE,"E31.0")]}),-1.0]])],"derivedFrom":subQ0})])],"isStart":false});}
            var Q7;
            {var subQ0=sQuery(id+"F0.wireOp",EDGE,"E32.MirrorCS");Q7=makeQuery(id+"F2.opExtrude","CAP_EDGE",EDGE,{"disambiguationData":[OSD([subQ0]),TDD([makeQuery(id+"F0.imprint","IMPRINT",EDGE,{"disambiguationData":[TD([[makeQuery(id+"F0.imprint","INTERSECT",VERTEX,{"derivedFrom":[sQuery(id+"F0.wireOp",EDGE,"E20.top"),subQ0]}),-1.0]])],"derivedFrom":subQ0})])],"isStart":false});}
            var Q8;
            {var subQ0=sQuery(id+"F0.wireOp",EDGE,"E31.0");Q8=makeQuery(id+"F2.opExtrude","CAP_EDGE",EDGE,{"disambiguationData":[OSD([subQ0]),TDD([makeQuery(id+"F0.imprint","IMPRINT",EDGE,{"disambiguationData":[TD([[makeQuery(id+"F0.imprint","INTERSECT",VERTEX,{"derivedFrom":[subQ0,sQuery(id+"F0.wireOp",EDGE,"E34.MirrorCS")]}),-1.0]])],"derivedFrom":subQ0})])],"isStart":false});}
            var Q9;
            {var subQ0=sQuery(id+"F0.wireOp",EDGE,"E26");Q9=makeQuery(id+"F2.opExtrude","CAP_EDGE",EDGE,{"disambiguationData":[OSD([subQ0]),TDD([makeQuery(id+"F0.imprint","IMPRINT",EDGE,{"disambiguationData":[TD([[makeQuery(id+"F0.imprint","INTERSECT",VERTEX,{"derivedFrom":[subQ0,sQuery(id+"F0.wireOp",EDGE,"E31.0")]}),-1.0]])],"derivedFrom":subQ0})])],"isStart":false});}
            var Q10;
            {var subQ0=sQuery(id+"F0.wireOp",EDGE,"E34.MirrorCS");Q10=makeQuery(id+"F2.opExtrude","CAP_EDGE",EDGE,{"disambiguationData":[OSD([subQ0]),TDD([makeQuery(id+"F0.imprint","IMPRINT",EDGE,{"disambiguationData":[TD([[makeQuery(id+"F0.imprint","INTERSECT",VERTEX,{"derivedFrom":[sQuery(id+"F0.wireOp",EDGE,"E31.0"),subQ0]}),-1.0]])],"derivedFrom":subQ0})])],"isStart":false});}
            var Q11;
            {var subQ0=sQuery(id+"F0.wireOp",EDGE,"E33.0");Q11=makeQuery(id+"F2.opExtrude","CAP_EDGE",EDGE,{"disambiguationData":[OSD([subQ0]),TDD([makeQuery(id+"F0.imprint","IMPRINT",EDGE,{"disambiguationData":[TD([[makeQuery(id+"F0.imprint","INTERSECT",VERTEX,{"derivedFrom":[subQ0,sQuery(id+"F0.wireOp",EDGE,"E36.MirrorCS")]}),-1.0]])],"derivedFrom":subQ0})])],"isStart":false});}
            var Q12;
            {var subQ0=sQuery(id+"F0.wireOp",EDGE,"E36.MirrorCS");Q12=makeQuery(id+"F2.opExtrude","CAP_EDGE",EDGE,{"disambiguationData":[OSD([subQ0]),TDD([makeQuery(id+"F0.imprint","IMPRINT",EDGE,{"disambiguationData":[TD([[makeQuery(id+"F0.imprint","INTERSECT",VERTEX,{"derivedFrom":[sQuery(id+"F0.wireOp",EDGE,"E33.0"),subQ0]}),-1.0]])],"derivedFrom":subQ0})])],"isStart":false});}
            var Q13;
            {var subQ0=sQuery(id+"F0.wireOp",EDGE,"E35.0");Q13=makeQuery(id+"F2.opExtrude","CAP_EDGE",EDGE,{"disambiguationData":[OSD([subQ0]),TDD([makeQuery(id+"F0.imprint","IMPRINT",EDGE,{"disambiguationData":[TD([[makeQuery(id+"F0.imprint","INTERSECT",VERTEX,{"derivedFrom":[subQ0,sQuery(id+"F0.wireOp",EDGE,"E38.0")]}),-1.0]])],"derivedFrom":subQ0})])],"isStart":false});}
            var Q14;
            {var subQ0=sQuery(id+"F0.wireOp",EDGE,"E38.0");Q14=makeQuery(id+"F2.opExtrude","CAP_EDGE",EDGE,{"disambiguationData":[OSD([subQ0]),TDD([makeQuery(id+"F0.imprint","IMPRINT",EDGE,{"disambiguationData":[TD([[makeQuery(id+"F0.imprint","INTERSECT",VERTEX,{"derivedFrom":[sQuery(id+"F0.wireOp",EDGE,"E35.0"),subQ0]}),-1.0]])],"derivedFrom":subQ0})])],"isStart":false});}
            var Q15;
            {var subQ0=sQuery(id+"F0.wireOp",EDGE,"E37.0");Q15=makeQuery(id+"F2.opExtrude","CAP_EDGE",EDGE,{"disambiguationData":[OSD([subQ0]),TDD([makeQuery(id+"F0.imprint","IMPRINT",EDGE,{"disambiguationData":[TD([[makeQuery(id+"F0.imprint","INTERSECT",VERTEX,{"derivedFrom":[subQ0,sQuery(id+"F0.wireOp",EDGE,"E40.0")]}),-1.0]])],"derivedFrom":subQ0})])],"isStart":false});}
            var Q16;
            {var subQ0=sQuery(id+"F0.wireOp",EDGE,"E40.0");Q16=makeQuery(id+"F2.opExtrude","CAP_EDGE",EDGE,{"disambiguationData":[OSD([subQ0]),TDD([makeQuery(id+"F0.imprint","IMPRINT",EDGE,{"disambiguationData":[TD([[makeQuery(id+"F0.imprint","INTERSECT",VERTEX,{"derivedFrom":[sQuery(id+"F0.wireOp",EDGE,"E37.0"),subQ0]}),-1.0]])],"derivedFrom":subQ0})])],"isStart":false});}
            var Q17;
            {var subQ0=sQuery(id+"F0.wireOp",EDGE,"E39.0");Q17=makeQuery(id+"F2.opExtrude","CAP_EDGE",EDGE,{"disambiguationData":[OSD([subQ0]),TDD([makeQuery(id+"F0.imprint","IMPRINT",EDGE,{"disambiguationData":[TD([[makeQuery(id+"F0.imprint","INTERSECT",VERTEX,{"derivedFrom":[subQ0,sQuery(id+"F0.wireOp",EDGE,"E44.0")]}),-1.0]])],"derivedFrom":subQ0})])],"isStart":false});}
            var Q18;
            {var subQ0=sQuery(id+"F0.wireOp",EDGE,"E44.0");Q18=makeQuery(id+"F2.opExtrude","CAP_EDGE",EDGE,{"disambiguationData":[OSD([subQ0]),TDD([makeQuery(id+"F0.imprint","IMPRINT",EDGE,{"disambiguationData":[TD([[makeQuery(id+"F0.imprint","INTERSECT",VERTEX,{"derivedFrom":[sQuery(id+"F0.wireOp",EDGE,"E39.0"),subQ0]}),-1.0]])],"derivedFrom":subQ0})])],"isStart":false});}
            var Q19;
            {var subQ0=sQuery(id+"F0.wireOp",EDGE,"E43.0");Q19=makeQuery(id+"F2.opExtrude","CAP_EDGE",EDGE,{"disambiguationData":[OSD([subQ0]),TDD([makeQuery(id+"F0.imprint","IMPRINT",EDGE,{"disambiguationData":[TD([[makeQuery(id+"F0.imprint","INTERSECT",VERTEX,{"derivedFrom":[sQuery(id+"F0.wireOp",EDGE,"E42.0"),subQ0]}),-1.0]])],"derivedFrom":subQ0})])],"isStart":false});}
            var Q20;
            {var subQ0=sQuery(id+"F0.wireOp",EDGE,"E42.0");Q20=makeQuery(id+"F2.opExtrude","CAP_EDGE",EDGE,{"disambiguationData":[OSD([subQ0]),TDD([makeQuery(id+"F0.imprint","IMPRINT",EDGE,{"disambiguationData":[TD([[makeQuery(id+"F0.imprint","INTERSECT",VERTEX,{"derivedFrom":[subQ0,sQuery(id+"F0.wireOp",EDGE,"E43.0")]}),-1.0]])],"derivedFrom":subQ0})])],"isStart":false});}
            var Q21;
            {var subQ0=sQuery(id+"F0.wireOp",EDGE,"E41.0");Q21=makeQuery(id+"F2.opExtrude","CAP_EDGE",EDGE,{"disambiguationData":[OSD([subQ0]),TDD([makeQuery(id+"F0.imprint","IMPRINT",EDGE,{"disambiguationData":[TD([[makeQuery(id+"F0.imprint","INTERSECT",VERTEX,{"derivedFrom":[sQuery(id+"F0.wireOp",EDGE,"E20.top"),subQ0]}),-1.0]])],"derivedFrom":subQ0})])],"isStart":false});}
            var Q22;
            {var subQ0=sQuery(id+"F0.wireOp",EDGE,"E27");Q22=makeQuery(id+"F2.opExtrude","CAP_EDGE",EDGE,{"disambiguationData":[OSD([subQ0]),TDD([makeQuery(id+"F0.imprint","IMPRINT",EDGE,{"disambiguationData":[TD([[makeQuery(id+"F0.imprint","INTERSECT",VERTEX,{"disambiguationData":[OD(1.0)],"derivedFrom":[sQuery(id+"F0.wireOp",EDGE,"E20.top"),subQ0]}),1.0]])],"derivedFrom":subQ0})])],"isStart":false});}
            var Q23;
            {var subQ0=sQuery(id+"F0.wireOp",EDGE,"E26");Q23=makeQuery(id+"F2.opExtrude","CAP_EDGE",EDGE,{"disambiguationData":[OSD([subQ0]),TDD([makeQuery(id+"F0.imprint","IMPRINT",EDGE,{"disambiguationData":[TD([[makeQuery(id+"F0.imprint","INTERSECT",VERTEX,{"derivedFrom":[subQ0,sQuery(id+"F0.wireOp",EDGE,"E42.0")]}),1.0]])],"derivedFrom":subQ0})])],"isStart":false});}
            var Q24;
            {var subQ0=sQuery(id+"F0.wireOp",EDGE,"E27");Q24=makeQuery(id+"F2.opExtrude","CAP_EDGE",EDGE,{"disambiguationData":[OSD([subQ0]),TDD([makeQuery(id+"F0.imprint","IMPRINT",EDGE,{"disambiguationData":[TD([[makeQuery(id+"F0.imprint","INTERSECT",VERTEX,{"derivedFrom":[subQ0,sQuery(id+"F0.wireOp",EDGE,"E43.0")]}),-1.0]])],"derivedFrom":subQ0})])],"isStart":false});}
            var Q25;
            {var subQ0=sQuery(id+"F0.wireOp",EDGE,"E27");Q25=makeQuery(id+"F2.opExtrude","CAP_EDGE",EDGE,{"disambiguationData":[OSD([subQ0]),TDD([makeQuery(id+"F0.imprint","IMPRINT",EDGE,{"disambiguationData":[TD([[makeQuery(id+"F0.imprint","INTERSECT",VERTEX,{"derivedFrom":[subQ0,sQuery(id+"F0.wireOp",EDGE,"E39.0")]}),-1.0]])],"derivedFrom":subQ0})])],"isStart":false});}
            var Q26;
            {var subQ0=sQuery(id+"F0.wireOp",EDGE,"E26");Q26=makeQuery(id+"F2.opExtrude","CAP_EDGE",EDGE,{"disambiguationData":[OSD([subQ0]),TDD([makeQuery(id+"F0.imprint","IMPRINT",EDGE,{"disambiguationData":[TD([[makeQuery(id+"F0.imprint","INTERSECT",VERTEX,{"derivedFrom":[subQ0,sQuery(id+"F0.wireOp",EDGE,"E39.0")]}),-1.0]])],"derivedFrom":subQ0})])],"isStart":false});}
            var Q27;
            {var subQ0=sQuery(id+"F0.wireOp",EDGE,"E26");Q27=makeQuery(id+"F2.opExtrude","CAP_EDGE",EDGE,{"disambiguationData":[OSD([subQ0]),TDD([makeQuery(id+"F0.imprint","IMPRINT",EDGE,{"disambiguationData":[TD([[makeQuery(id+"F0.imprint","INTERSECT",VERTEX,{"derivedFrom":[subQ0,sQuery(id+"F0.wireOp",EDGE,"E37.0")]}),-1.0]])],"derivedFrom":subQ0})])],"isStart":false});}
            var Q28;
            {var subQ0=sQuery(id+"F0.wireOp",EDGE,"E27");Q28=makeQuery(id+"F2.opExtrude","CAP_EDGE",EDGE,{"disambiguationData":[OSD([subQ0]),TDD([makeQuery(id+"F0.imprint","IMPRINT",EDGE,{"disambiguationData":[TD([[makeQuery(id+"F0.imprint","INTERSECT",VERTEX,{"derivedFrom":[subQ0,sQuery(id+"F0.wireOp",EDGE,"E37.0")]}),-1.0]])],"derivedFrom":subQ0})])],"isStart":false});}
            var Q29;
            {var subQ0=sQuery(id+"F0.wireOp",EDGE,"E26");Q29=makeQuery(id+"F2.opExtrude","CAP_EDGE",EDGE,{"disambiguationData":[OSD([subQ0]),TDD([makeQuery(id+"F0.imprint","IMPRINT",EDGE,{"disambiguationData":[TD([[makeQuery(id+"F0.imprint","INTERSECT",VERTEX,{"derivedFrom":[subQ0,sQuery(id+"F0.wireOp",EDGE,"E35.0")]}),-1.0]])],"derivedFrom":subQ0})])],"isStart":false});}
            var Q30;
            {var subQ0=sQuery(id+"F0.wireOp",EDGE,"E27");Q30=makeQuery(id+"F2.opExtrude","CAP_EDGE",EDGE,{"disambiguationData":[OSD([subQ0]),TDD([makeQuery(id+"F0.imprint","IMPRINT",EDGE,{"disambiguationData":[TD([[makeQuery(id+"F0.imprint","INTERSECT",VERTEX,{"derivedFrom":[subQ0,sQuery(id+"F0.wireOp",EDGE,"E35.0")]}),-1.0]])],"derivedFrom":subQ0})])],"isStart":false});}
            var Q31;
            {var subQ0=sQuery(id+"F0.wireOp",EDGE,"E27");Q31=makeQuery(id+"F2.opExtrude","CAP_EDGE",EDGE,{"disambiguationData":[OSD([subQ0]),TDD([makeQuery(id+"F0.imprint","IMPRINT",EDGE,{"disambiguationData":[TD([[makeQuery(id+"F0.imprint","INTERSECT",VERTEX,{"derivedFrom":[subQ0,sQuery(id+"F0.wireOp",EDGE,"E33.0")]}),-1.0]])],"derivedFrom":subQ0})])],"isStart":false});}
            var Q32;
            {var subQ0=sQuery(id+"F0.wireOp",EDGE,"E26");Q32=makeQuery(id+"F2.opExtrude","CAP_EDGE",EDGE,{"disambiguationData":[OSD([subQ0]),TDD([makeQuery(id+"F0.imprint","IMPRINT",EDGE,{"disambiguationData":[TD([[makeQuery(id+"F0.imprint","INTERSECT",VERTEX,{"derivedFrom":[subQ0,sQuery(id+"F0.wireOp",EDGE,"E33.0")]}),-1.0]])],"derivedFrom":subQ0})])],"isStart":false});}
            var Q33;
            {var subQ0=sQuery(id+"F0.wireOp",EDGE,"E26");Q33=makeQuery(id+"F2.opExtrude","CAP_EDGE",EDGE,{"disambiguationData":[OSD([subQ0]),TDD([makeQuery(id+"F0.imprint","IMPRINT",EDGE,{"disambiguationData":[TD([[makeQuery(id+"F0.imprint","INTERSECT",VERTEX,{"disambiguationData":[OD(1.0)],"derivedFrom":[sQuery(id+"F0.wireOp",EDGE,"E20.top"),subQ0]}),1.0]])],"derivedFrom":subQ0})])],"isStart":false});}
            var Q34;
            {var subQ0=sQuery(id+"F0.wireOp",EDGE,"E41.0");Q34=makeQuery(id+"F2.opExtrude","CAP_EDGE",EDGE,{"disambiguationData":[OSD([subQ0]),TDD([makeQuery(id+"F0.imprint","IMPRINT",EDGE,{"disambiguationData":[TD([[makeQuery(id+"F0.imprint","INTERSECT",VERTEX,{"derivedFrom":[sQuery(id+"F0.wireOp",EDGE,"E26"),subQ0]}),-1.0]])],"derivedFrom":subQ0})])],"isStart":false});}
            var Q35;
            {var subQ0=sQuery(id+"F0.wireOp",EDGE,"E42.0");Q35=makeQuery(id+"F2.opExtrude","CAP_EDGE",EDGE,{"disambiguationData":[OSD([subQ0]),TDD([makeQuery(id+"F0.imprint","IMPRINT",EDGE,{"disambiguationData":[TD([[makeQuery(id+"F0.imprint","INTERSECT",VERTEX,{"derivedFrom":[sQuery(id+"F0.wireOp",EDGE,"E26"),subQ0]}),-1.0]])],"derivedFrom":subQ0})])],"isStart":false});}
            var Q36;
            {var subQ0=sQuery(id+"F0.wireOp",EDGE,"E43.0");Q36=makeQuery(id+"F2.opExtrude","CAP_EDGE",EDGE,{"disambiguationData":[OSD([subQ0]),TDD([makeQuery(id+"F0.imprint","IMPRINT",EDGE,{"disambiguationData":[TD([[makeQuery(id+"F0.imprint","INTERSECT",VERTEX,{"derivedFrom":[sQuery(id+"F0.wireOp",EDGE,"E26"),subQ0]}),-1.0]])],"derivedFrom":subQ0})])],"isStart":false});}
            var Q37;
            {var subQ0=sQuery(id+"F0.wireOp",EDGE,"E44.0");Q37=makeQuery(id+"F2.opExtrude","CAP_EDGE",EDGE,{"disambiguationData":[OSD([subQ0]),TDD([makeQuery(id+"F0.imprint","IMPRINT",EDGE,{"disambiguationData":[TD([[makeQuery(id+"F0.imprint","INTERSECT",VERTEX,{"derivedFrom":[sQuery(id+"F0.wireOp",EDGE,"E26"),subQ0]}),-1.0]])],"derivedFrom":subQ0})])],"isStart":false});}
            var Q38;
            {var subQ0=sQuery(id+"F0.wireOp",EDGE,"E39.0");Q38=makeQuery(id+"F2.opExtrude","CAP_EDGE",EDGE,{"disambiguationData":[OSD([subQ0]),TDD([makeQuery(id+"F0.imprint","IMPRINT",EDGE,{"disambiguationData":[TD([[makeQuery(id+"F0.imprint","INTERSECT",VERTEX,{"derivedFrom":[sQuery(id+"F0.wireOp",EDGE,"E26"),subQ0]}),-1.0]])],"derivedFrom":subQ0})])],"isStart":false});}
            var Q39;
            {var subQ0=sQuery(id+"F0.wireOp",EDGE,"E40.0");Q39=makeQuery(id+"F2.opExtrude","CAP_EDGE",EDGE,{"disambiguationData":[OSD([subQ0]),TDD([makeQuery(id+"F0.imprint","IMPRINT",EDGE,{"disambiguationData":[TD([[makeQuery(id+"F0.imprint","INTERSECT",VERTEX,{"derivedFrom":[sQuery(id+"F0.wireOp",EDGE,"E26"),subQ0]}),-1.0]])],"derivedFrom":subQ0})])],"isStart":false});}
            var Q40;
            {var subQ0=sQuery(id+"F0.wireOp",EDGE,"E38.0");Q40=makeQuery(id+"F2.opExtrude","CAP_EDGE",EDGE,{"disambiguationData":[OSD([subQ0]),TDD([makeQuery(id+"F0.imprint","IMPRINT",EDGE,{"disambiguationData":[TD([[makeQuery(id+"F0.imprint","INTERSECT",VERTEX,{"derivedFrom":[sQuery(id+"F0.wireOp",EDGE,"E26"),subQ0]}),-1.0]])],"derivedFrom":subQ0})])],"isStart":false});}
            var Q41;
            {var subQ0=sQuery(id+"F0.wireOp",EDGE,"E35.0");Q41=makeQuery(id+"F2.opExtrude","CAP_EDGE",EDGE,{"disambiguationData":[OSD([subQ0]),TDD([makeQuery(id+"F0.imprint","IMPRINT",EDGE,{"disambiguationData":[TD([[makeQuery(id+"F0.imprint","INTERSECT",VERTEX,{"derivedFrom":[sQuery(id+"F0.wireOp",EDGE,"E26"),subQ0]}),-1.0]])],"derivedFrom":subQ0})])],"isStart":false});}
            var Q42;
            {var subQ0=sQuery(id+"F0.wireOp",EDGE,"E36.MirrorCS");Q42=makeQuery(id+"F2.opExtrude","CAP_EDGE",EDGE,{"disambiguationData":[OSD([subQ0]),TDD([makeQuery(id+"F0.imprint","IMPRINT",EDGE,{"disambiguationData":[TD([[makeQuery(id+"F0.imprint","INTERSECT",VERTEX,{"derivedFrom":[sQuery(id+"F0.wireOp",EDGE,"E26"),subQ0]}),-1.0]])],"derivedFrom":subQ0})])],"isStart":false});}
            var Q43;
            {var subQ0=sQuery(id+"F0.wireOp",EDGE,"E33.0");Q43=makeQuery(id+"F2.opExtrude","CAP_EDGE",EDGE,{"disambiguationData":[OSD([subQ0]),TDD([makeQuery(id+"F0.imprint","IMPRINT",EDGE,{"disambiguationData":[TD([[makeQuery(id+"F0.imprint","INTERSECT",VERTEX,{"derivedFrom":[sQuery(id+"F0.wireOp",EDGE,"E26"),subQ0]}),-1.0]])],"derivedFrom":subQ0})])],"isStart":false});}
            var Q44;
            {var subQ0=sQuery(id+"F0.wireOp",EDGE,"E34.MirrorCS");Q44=makeQuery(id+"F2.opExtrude","CAP_EDGE",EDGE,{"disambiguationData":[OSD([subQ0]),TDD([makeQuery(id+"F0.imprint","IMPRINT",EDGE,{"disambiguationData":[TD([[makeQuery(id+"F0.imprint","INTERSECT",VERTEX,{"derivedFrom":[sQuery(id+"F0.wireOp",EDGE,"E26"),subQ0]}),-1.0]])],"derivedFrom":subQ0})])],"isStart":false});}
            var Q45;
            {var subQ0=sQuery(id+"F0.wireOp",EDGE,"E25");Q45=makeQuery(id+"F2.opExtrude","CAP_EDGE",EDGE,{"disambiguationData":[OSD([subQ0]),TDD([makeQuery(id+"F0.imprint","IMPRINT",EDGE,{"disambiguationData":[TD([[makeQuery(id+"F0.imprint","INTERSECT",VERTEX,{"derivedFrom":[subQ0,sQuery(id+"F0.wireOp",EDGE,"E31.0")]}),-1.0]])],"derivedFrom":subQ0})])],"isStart":false});}
            var Q46;
            {var subQ0=sQuery(id+"F0.wireOp",EDGE,"E24");Q46=makeQuery(id+"F2.opExtrude","CAP_EDGE",EDGE,{"disambiguationData":[OSD([subQ0]),TDD([makeQuery(id+"F0.imprint","IMPRINT",EDGE,{"disambiguationData":[TD([[makeQuery(id+"F0.imprint","INTERSECT",VERTEX,{"derivedFrom":[subQ0,sQuery(id+"F0.wireOp",EDGE,"E31.0")]}),-1.0]])],"derivedFrom":subQ0})])],"isStart":false});}
            var Q47;
            {var subQ0=sQuery(id+"F0.wireOp",EDGE,"E25");Q47=makeQuery(id+"F2.opExtrude","CAP_EDGE",EDGE,{"disambiguationData":[OSD([subQ0]),TDD([makeQuery(id+"F0.imprint","IMPRINT",EDGE,{"disambiguationData":[TD([[makeQuery(id+"F0.imprint","INTERSECT",VERTEX,{"derivedFrom":[subQ0,sQuery(id+"F0.wireOp",EDGE,"E33.0")]}),-1.0]])],"derivedFrom":subQ0})])],"isStart":false});}
            var Q48;
            {var subQ0=sQuery(id+"F0.wireOp",EDGE,"E24");Q48=makeQuery(id+"F2.opExtrude","CAP_EDGE",EDGE,{"disambiguationData":[OSD([subQ0]),TDD([makeQuery(id+"F0.imprint","IMPRINT",EDGE,{"disambiguationData":[TD([[makeQuery(id+"F0.imprint","INTERSECT",VERTEX,{"derivedFrom":[subQ0,sQuery(id+"F0.wireOp",EDGE,"E33.0")]}),-1.0]])],"derivedFrom":subQ0})])],"isStart":false});}
            var Q49;
            {var subQ0=sQuery(id+"F0.wireOp",EDGE,"E25");Q49=makeQuery(id+"F2.opExtrude","CAP_EDGE",EDGE,{"disambiguationData":[OSD([subQ0]),TDD([makeQuery(id+"F0.imprint","IMPRINT",EDGE,{"disambiguationData":[TD([[makeQuery(id+"F0.imprint","INTERSECT",VERTEX,{"derivedFrom":[subQ0,sQuery(id+"F0.wireOp",EDGE,"E35.0")]}),-1.0]])],"derivedFrom":subQ0})])],"isStart":false});}
            var Q50;
            {var subQ0=sQuery(id+"F0.wireOp",EDGE,"E24");Q50=makeQuery(id+"F2.opExtrude","CAP_EDGE",EDGE,{"disambiguationData":[OSD([subQ0]),TDD([makeQuery(id+"F0.imprint","IMPRINT",EDGE,{"disambiguationData":[TD([[makeQuery(id+"F0.imprint","INTERSECT",VERTEX,{"derivedFrom":[subQ0,sQuery(id+"F0.wireOp",EDGE,"E35.0")]}),-1.0]])],"derivedFrom":subQ0})])],"isStart":false});}
            var Q51;
            {var subQ0=sQuery(id+"F0.wireOp",EDGE,"E25");Q51=makeQuery(id+"F2.opExtrude","CAP_EDGE",EDGE,{"disambiguationData":[OSD([subQ0]),TDD([makeQuery(id+"F0.imprint","IMPRINT",EDGE,{"disambiguationData":[TD([[makeQuery(id+"F0.imprint","INTERSECT",VERTEX,{"derivedFrom":[subQ0,sQuery(id+"F0.wireOp",EDGE,"E37.0")]}),-1.0]])],"derivedFrom":subQ0})])],"isStart":false});}
            var Q52;
            {var subQ0=sQuery(id+"F0.wireOp",EDGE,"E24");Q52=makeQuery(id+"F2.opExtrude","CAP_EDGE",EDGE,{"disambiguationData":[OSD([subQ0]),TDD([makeQuery(id+"F0.imprint","IMPRINT",EDGE,{"disambiguationData":[TD([[makeQuery(id+"F0.imprint","INTERSECT",VERTEX,{"derivedFrom":[subQ0,sQuery(id+"F0.wireOp",EDGE,"E37.0")]}),-1.0]])],"derivedFrom":subQ0})])],"isStart":false});}
            var Q53;
            {var subQ0=sQuery(id+"F0.wireOp",EDGE,"E25");Q53=makeQuery(id+"F2.opExtrude","CAP_EDGE",EDGE,{"disambiguationData":[OSD([subQ0]),TDD([makeQuery(id+"F0.imprint","IMPRINT",EDGE,{"disambiguationData":[TD([[makeQuery(id+"F0.imprint","INTERSECT",VERTEX,{"derivedFrom":[subQ0,sQuery(id+"F0.wireOp",EDGE,"E39.0")]}),-1.0]])],"derivedFrom":subQ0})])],"isStart":false});}
            var Q54;
            {var subQ0=sQuery(id+"F0.wireOp",EDGE,"E24");Q54=makeQuery(id+"F2.opExtrude","CAP_EDGE",EDGE,{"disambiguationData":[OSD([subQ0]),TDD([makeQuery(id+"F0.imprint","IMPRINT",EDGE,{"disambiguationData":[TD([[makeQuery(id+"F0.imprint","INTERSECT",VERTEX,{"derivedFrom":[subQ0,sQuery(id+"F0.wireOp",EDGE,"E39.0")]}),-1.0]])],"derivedFrom":subQ0})])],"isStart":false});}
            var Q55;
            {var subQ0=sQuery(id+"F0.wireOp",EDGE,"E25");Q55=makeQuery(id+"F2.opExtrude","CAP_EDGE",EDGE,{"disambiguationData":[OSD([subQ0]),TDD([makeQuery(id+"F0.imprint","IMPRINT",EDGE,{"disambiguationData":[TD([[makeQuery(id+"F0.imprint","INTERSECT",VERTEX,{"derivedFrom":[subQ0,sQuery(id+"F0.wireOp",EDGE,"E43.0")]}),-1.0]])],"derivedFrom":subQ0})])],"isStart":false});}
            var Q56;
            {var subQ0=sQuery(id+"F0.wireOp",EDGE,"E24");Q56=makeQuery(id+"F2.opExtrude","CAP_EDGE",EDGE,{"disambiguationData":[OSD([subQ0]),TDD([makeQuery(id+"F0.imprint","IMPRINT",EDGE,{"disambiguationData":[TD([[makeQuery(id+"F0.imprint","INTERSECT",VERTEX,{"derivedFrom":[subQ0,sQuery(id+"F0.wireOp",EDGE,"E42.0")]}),1.0]])],"derivedFrom":subQ0})])],"isStart":false});}
            var Q57;
            {var subQ0=sQuery(id+"F0.wireOp",EDGE,"E24");Q57=makeQuery(id+"F2.opExtrude","CAP_EDGE",EDGE,{"disambiguationData":[OSD([subQ0]),TDD([makeQuery(id+"F0.imprint","IMPRINT",EDGE,{"disambiguationData":[TD([[makeQuery(id+"F0.imprint","INTERSECT",VERTEX,{"disambiguationData":[OD(1.0)],"derivedFrom":[sQuery(id+"F0.wireOp",EDGE,"E20.top"),subQ0]}),1.0]])],"derivedFrom":subQ0})])],"isStart":false});}
            var Q58;
            {var subQ0=sQuery(id+"F0.wireOp",EDGE,"E41.0");Q58=makeQuery(id+"F2.opExtrude","CAP_EDGE",EDGE,{"disambiguationData":[OSD([subQ0]),TDD([makeQuery(id+"F0.imprint","IMPRINT",EDGE,{"disambiguationData":[TD([[makeQuery(id+"F0.imprint","INTERSECT",VERTEX,{"derivedFrom":[sQuery(id+"F0.wireOp",EDGE,"E24"),subQ0]}),-1.0]])],"derivedFrom":subQ0})])],"isStart":false});}
            var Q59;
            {var subQ0=sQuery(id+"F0.wireOp",EDGE,"E42.0");Q59=makeQuery(id+"F2.opExtrude","CAP_EDGE",EDGE,{"disambiguationData":[OSD([subQ0]),TDD([makeQuery(id+"F0.imprint","IMPRINT",EDGE,{"disambiguationData":[TD([[makeQuery(id+"F0.imprint","INTERSECT",VERTEX,{"derivedFrom":[sQuery(id+"F0.wireOp",EDGE,"E24"),subQ0]}),-1.0]])],"derivedFrom":subQ0})])],"isStart":false});}
            var Q60;
            {var subQ0=sQuery(id+"F0.wireOp",EDGE,"E25");Q60=makeQuery(id+"F2.opExtrude","CAP_EDGE",EDGE,{"disambiguationData":[OSD([subQ0]),TDD([makeQuery(id+"F0.imprint","IMPRINT",EDGE,{"disambiguationData":[TD([[makeQuery(id+"F0.imprint","INTERSECT",VERTEX,{"disambiguationData":[OD(1.0)],"derivedFrom":[sQuery(id+"F0.wireOp",EDGE,"E20.top"),subQ0]}),1.0]])],"derivedFrom":subQ0})])],"isStart":false});}
            var Q61;
            {var subQ0=sQuery(id+"F0.wireOp",EDGE,"E43.0");Q61=makeQuery(id+"F2.opExtrude","CAP_EDGE",EDGE,{"disambiguationData":[OSD([subQ0]),TDD([makeQuery(id+"F0.imprint","IMPRINT",EDGE,{"disambiguationData":[TD([[makeQuery(id+"F0.imprint","INTERSECT",VERTEX,{"derivedFrom":[sQuery(id+"F0.wireOp",EDGE,"E24"),subQ0]}),-1.0]])],"derivedFrom":subQ0})])],"isStart":false});}
            var Q62;
            {var subQ0=sQuery(id+"F0.wireOp",EDGE,"E44.0");Q62=makeQuery(id+"F2.opExtrude","CAP_EDGE",EDGE,{"disambiguationData":[OSD([subQ0]),TDD([makeQuery(id+"F0.imprint","IMPRINT",EDGE,{"disambiguationData":[TD([[makeQuery(id+"F0.imprint","INTERSECT",VERTEX,{"derivedFrom":[sQuery(id+"F0.wireOp",EDGE,"E24"),subQ0]}),-1.0]])],"derivedFrom":subQ0})])],"isStart":false});}
            var Q63;
            {var subQ0=sQuery(id+"F0.wireOp",EDGE,"E39.0");Q63=makeQuery(id+"F2.opExtrude","CAP_EDGE",EDGE,{"disambiguationData":[OSD([subQ0]),TDD([makeQuery(id+"F0.imprint","IMPRINT",EDGE,{"disambiguationData":[TD([[makeQuery(id+"F0.imprint","INTERSECT",VERTEX,{"derivedFrom":[sQuery(id+"F0.wireOp",EDGE,"E24"),subQ0]}),-1.0]])],"derivedFrom":subQ0})])],"isStart":false});}
            var Q64;
            {var subQ0=sQuery(id+"F0.wireOp",EDGE,"E40.0");Q64=makeQuery(id+"F2.opExtrude","CAP_EDGE",EDGE,{"disambiguationData":[OSD([subQ0]),TDD([makeQuery(id+"F0.imprint","IMPRINT",EDGE,{"disambiguationData":[TD([[makeQuery(id+"F0.imprint","INTERSECT",VERTEX,{"derivedFrom":[sQuery(id+"F0.wireOp",EDGE,"E24"),subQ0]}),-1.0]])],"derivedFrom":subQ0})])],"isStart":false});}
            var Q65;
            {var subQ0=sQuery(id+"F0.wireOp",EDGE,"E37.0");Q65=makeQuery(id+"F2.opExtrude","CAP_EDGE",EDGE,{"disambiguationData":[OSD([subQ0]),TDD([makeQuery(id+"F0.imprint","IMPRINT",EDGE,{"disambiguationData":[TD([[makeQuery(id+"F0.imprint","INTERSECT",VERTEX,{"derivedFrom":[sQuery(id+"F0.wireOp",EDGE,"E26"),subQ0]}),-1.0]])],"derivedFrom":subQ0})])],"isStart":false});}
            var Q66;
            {var subQ0=sQuery(id+"F0.wireOp",EDGE,"E37.0");Q66=makeQuery(id+"F2.opExtrude","CAP_EDGE",EDGE,{"disambiguationData":[OSD([subQ0]),TDD([makeQuery(id+"F0.imprint","IMPRINT",EDGE,{"disambiguationData":[TD([[makeQuery(id+"F0.imprint","INTERSECT",VERTEX,{"derivedFrom":[sQuery(id+"F0.wireOp",EDGE,"E24"),subQ0]}),-1.0]])],"derivedFrom":subQ0})])],"isStart":false});}
            var Q67;
            {var subQ0=sQuery(id+"F0.wireOp",EDGE,"E38.0");Q67=makeQuery(id+"F2.opExtrude","CAP_EDGE",EDGE,{"disambiguationData":[OSD([subQ0]),TDD([makeQuery(id+"F0.imprint","IMPRINT",EDGE,{"disambiguationData":[TD([[makeQuery(id+"F0.imprint","INTERSECT",VERTEX,{"derivedFrom":[sQuery(id+"F0.wireOp",EDGE,"E24"),subQ0]}),-1.0]])],"derivedFrom":subQ0})])],"isStart":false});}
            var Q68;
            {var subQ0=sQuery(id+"F0.wireOp",EDGE,"E35.0");Q68=makeQuery(id+"F2.opExtrude","CAP_EDGE",EDGE,{"disambiguationData":[OSD([subQ0]),TDD([makeQuery(id+"F0.imprint","IMPRINT",EDGE,{"disambiguationData":[TD([[makeQuery(id+"F0.imprint","INTERSECT",VERTEX,{"derivedFrom":[sQuery(id+"F0.wireOp",EDGE,"E24"),subQ0]}),-1.0]])],"derivedFrom":subQ0})])],"isStart":false});}
            var Q69;
            {var subQ0=sQuery(id+"F0.wireOp",EDGE,"E36.MirrorCS");Q69=makeQuery(id+"F2.opExtrude","CAP_EDGE",EDGE,{"disambiguationData":[OSD([subQ0]),TDD([makeQuery(id+"F0.imprint","IMPRINT",EDGE,{"disambiguationData":[TD([[makeQuery(id+"F0.imprint","INTERSECT",VERTEX,{"derivedFrom":[sQuery(id+"F0.wireOp",EDGE,"E24"),subQ0]}),-1.0]])],"derivedFrom":subQ0})])],"isStart":false});}
            var Q70;
            {var subQ0=sQuery(id+"F0.wireOp",EDGE,"E33.0");Q70=makeQuery(id+"F2.opExtrude","CAP_EDGE",EDGE,{"disambiguationData":[OSD([subQ0]),TDD([makeQuery(id+"F0.imprint","IMPRINT",EDGE,{"disambiguationData":[TD([[makeQuery(id+"F0.imprint","INTERSECT",VERTEX,{"derivedFrom":[sQuery(id+"F0.wireOp",EDGE,"E24"),subQ0]}),-1.0]])],"derivedFrom":subQ0})])],"isStart":false});}
            var Q71;
            {var subQ0=sQuery(id+"F0.wireOp",EDGE,"E34.MirrorCS");Q71=makeQuery(id+"F2.opExtrude","CAP_EDGE",EDGE,{"disambiguationData":[OSD([subQ0]),TDD([makeQuery(id+"F0.imprint","IMPRINT",EDGE,{"disambiguationData":[TD([[makeQuery(id+"F0.imprint","INTERSECT",VERTEX,{"derivedFrom":[sQuery(id+"F0.wireOp",EDGE,"E24"),subQ0]}),-1.0]])],"derivedFrom":subQ0})])],"isStart":false});}
            var Q72;
            {var subQ0=sQuery(id+"F0.wireOp",EDGE,"E31.0");Q72=makeQuery(id+"F2.opExtrude","CAP_EDGE",EDGE,{"disambiguationData":[OSD([subQ0]),TDD([makeQuery(id+"F0.imprint","IMPRINT",EDGE,{"disambiguationData":[TD([[makeQuery(id+"F0.imprint","INTERSECT",VERTEX,{"derivedFrom":[sQuery(id+"F0.wireOp",EDGE,"E24"),subQ0]}),-1.0]])],"derivedFrom":subQ0})])],"isStart":false});}
            var Q73;
            {var subQ0=sQuery(id+"F0.wireOp",EDGE,"E27");Q73=makeQuery(id+"F2.opExtrude","CAP_EDGE",EDGE,{"disambiguationData":[OSD([subQ0]),TDD([makeQuery(id+"F0.imprint","IMPRINT",EDGE,{"disambiguationData":[TD([[makeQuery(id+"F0.imprint","INTERSECT",VERTEX,{"disambiguationData":[OD(0.0)],"derivedFrom":[sQuery(id+"F0.wireOp",EDGE,"E20.top"),subQ0]}),-1.0]])],"derivedFrom":subQ0})])],"isStart":false});}
            fillet(context, id + "F5", {"entities" : qUnion([Q0, Q1, Q2, Q3, Q4, Q5, Q6, Q7, Q8, Q9, Q10, Q11, Q12, Q13, Q14, Q15, Q16, Q17, Q18, Q19, Q20, Q21, Q22, Q23, Q24, Q25, Q26, Q27, Q28, Q29, Q30, Q31, Q32, Q33, Q34, Q35, Q36, Q37, Q38, Q39, Q40, Q41, Q42, Q43, Q44, Q45, Q46, Q47, Q48, Q49, Q50, Q51, Q52, Q53, Q54, Q55, Q56, Q57, Q58, Q59, Q60, Q61, Q62, Q63, Q64, Q65, Q66, Q67, Q68, Q69, Q70, Q71, Q72, Q73]), "radius" : 0.5 * mm, "tangentPropagation" : true, "allowEdgeOverflow" : false});
        }
        {
            var Q0;
            Q0=makeQuery(id+"F1.opExtrude","SWEPT_FACE",FACE,{"disambiguationData":[OSD([sQuery(id+"F0.wireOp",EDGE,"E4")])]});
            var sketch = newSketch(context, id + "F6", { "sketchPlane" : qUnion([Q0])});
            skLineSegment(sketch, "E45.0", {"start": v(-19.33, 1.5) * mm, "end": v(-19.33, 0) * mm});
            skArc(sketch, "E45.1", {"start": v(-20.33, 1.5) * mm, "mid": v(-19.83, 2) * mm, "end": v(-19.33, 1.5) * mm});
            skLineSegment(sketch, "E45.2", {"start": v(-20.33, 1.5) * mm, "end": v(-20.33, 0) * mm});
            skLineSegment(sketch, "E46", {"start": v(-20.33, 0) * mm, "end": v(-19.33, 0) * mm});
            skLineSegment(sketch, "E47.0", {"start": v(-40.67, 1.5) * mm, "end": v(-40.67, 0) * mm});
            skArc(sketch, "E47.1", {"start": v(-40.67, 1.5) * mm, "mid": v(-40.17, 2) * mm, "end": v(-39.67, 1.5) * mm});
            skLineSegment(sketch, "E47.2", {"start": v(-39.67, 1.5) * mm, "end": v(-39.67, 0) * mm});
            skLineSegment(sketch, "E48", {"start": v(-40.67, 0) * mm, "end": v(-39.67, 0) * mm});
            skSolve(sketch);
        }
        {
            var Q0;
            Q0=qSketchRegion(id+"F6",true);
            var Q1;
            Q1=makeQuery(id+"F1.opExtrude","SWEPT_FACE",FACE,{"disambiguationData":[OSD([sQuery(id+"F0.wireOp",EDGE,"E8")])]});
            var Q2;
            Q2=makeQuery(id+"F1.opExtrude","SWEPT_FACE",FACE,{"disambiguationData":[OSD([sQuery(id+"F0.wireOp",EDGE,"E6")])]});
            extrude(context, id + "F7", {"entities" : qUnion([Q0]), "operationType" : NewBodyOperationType.ADD, "endBound" : BoundingType.UP_TO_SURFACE, "endBoundEntityFace" : qUnion([Q1]), "depth" : 25 * mm});
        }
        {
            var Q0;
            Q0=makeQuery(id+"F1.opExtrude","SWEPT_FACE",FACE,{"disambiguationData":[OSD([sQuery(id+"F0.wireOp",EDGE,"E6")])]});
            var sketch = newSketch(context, id + "F8", { "sketchPlane" : qUnion([Q0])});
            skLineSegment(sketch, "E49.0", {"start": v(40.67, 1.5) * mm, "end": v(40.67, 0) * mm});
            skArc(sketch, "E49.1", {"start": v(39.67, 1.5) * mm, "mid": v(40.17, 2) * mm, "end": v(40.67, 1.5) * mm});
            skLineSegment(sketch, "E49.2", {"start": v(39.67, 1.5) * mm, "end": v(39.67, 0) * mm});
            skLineSegment(sketch, "E50.0", {"start": v(19.33, 1.5) * mm, "end": v(19.33, 0) * mm});
            skArc(sketch, "E50.1", {"start": v(19.33, 1.5) * mm, "mid": v(19.83, 2) * mm, "end": v(20.33, 1.5) * mm});
            skLineSegment(sketch, "E50.2", {"start": v(20.33, 1.5) * mm, "end": v(20.33, 0) * mm});
            skLineSegment(sketch, "E51", {"start": v(19.33, 0) * mm, "end": v(20.33, 0) * mm});
            skLineSegment(sketch, "E52", {"start": v(39.67, 0) * mm, "end": v(40.67, 0) * mm});
            skSolve(sketch);
        }
        {
            var Q0;
            Q0=qSketchRegion(id+"F8",true);
            extrude(context, id + "F9", {"entities" : qUnion([Q0]), "operationType" : NewBodyOperationType.ADD, "endBound" : BoundingType.UP_TO_NEXT, "depth" : 25 * mm});
        }
        {
            var Q0;
            Q0=qCreatedBy(makeId("Top.planeOp"),FACE);
            var sketch = newSketch(context, id + "F10", { "sketchPlane" : qUnion([Q0])});
            skPoint(sketch, "E53.0", {"position": v(62, 63) * mm});
            skLineSegment(sketch, "E54", {"start": v(62, 63) * mm, "end": v(67.5, 63) * mm});
            skLineSegment(sketch, "E55", {"start": v(67.5, 63) * mm, "end": v(67.5, -3) * mm});
            skPoint(sketch, "E56.0", {"position": v(59, 60) * mm});
            skLineSegment(sketch, "E57.0", {"start": v(62, -3) * mm, "end": v(62, 63) * mm});
            skLineSegment(sketch, "E58", {"start": v(62, 60) * mm, "end": v(67.5, 60) * mm});
            skLineSegment(sketch, "E59", {"start": v(67.5, -3) * mm, "end": v(62, -3) * mm});
            skPoint(sketch, "E60.0", {"position": v(59, 0) * mm});
            skLineSegment(sketch, "E61", {"start": v(62, 0) * mm, "end": v(67.5, 0) * mm});
            skSolve(sketch);
        }
        {
            var Q0;
            {var subQ0=sQuery(id+"F10.wireOp",EDGE,"E54");Q0=makeQuery(id+"F10.imprint","IMPRINT",FACE,{"disambiguationData":[TD([[makeQuery(id+"F10.imprint","IMPRINT",EDGE,{"derivedFrom":subQ0}),-1.0]])]});}
            var Q1;
            {var subQ0=sQuery(id+"F10.wireOp",EDGE,"E59");Q1=makeQuery(id+"F10.imprint","IMPRINT",FACE,{"disambiguationData":[TD([[makeQuery(id+"F10.imprint","IMPRINT",EDGE,{"derivedFrom":subQ0}),-1.0]])]});}
            var Q2;
            Q2=makeQuery(id+"F1.opExtrude","CAP_FACE",FACE,{"disambiguationData":[OSD([sQuery(id+"F0.wireOp",EDGE,"E0.bottom"),sQuery(id+"F0.wireOp",EDGE,"E0.top"),sQuery(id+"F0.wireOp",EDGE,"E0.left"),sQuery(id+"F0.wireOp",EDGE,"E0.right"),sQuery(id+"F0.wireOp",EDGE,"E4"),sQuery(id+"F0.wireOp",EDGE,"E6"),sQuery(id+"F0.wireOp",EDGE,"E7"),sQuery(id+"F0.wireOp",EDGE,"E8"),sQuery(id+"F0.wireOp",EDGE,"E11"),sQuery(id+"F0.wireOp",EDGE,"E12"),sQuery(id+"F0.wireOp",EDGE,"E19.top"),sQuery(id+"F0.wireOp",EDGE,"E19.left"),sQuery(id+"F0.wireOp",EDGE,"E19.right"),sQuery(id+"F0.wireOp",EDGE,"E20.top"),sQuery(id+"F0.wireOp",EDGE,"E20.left"),sQuery(id+"F0.wireOp",EDGE,"E20.right"),sQuery(id+"F0.wireOp",EDGE,"E22"),sQuery(id+"F0.wireOp",EDGE,"E23")])],"isStart":false});
            extrude(context, id + "F11", {"entities" : qUnion([Q0, Q1]), "operationType" : NewBodyOperationType.ADD, "endBound" : BoundingType.UP_TO_SURFACE, "endBoundEntityFace" : qUnion([Q2]), "depth" : 25 * mm, "offsetDistance" : 25 * mm});
        }
        {
            var Q0;
            {var subQ0=sQuery(id+"F10.wireOp",EDGE,"E55");Q0=makeQuery(id+"F11.opExtrude","SWEPT_FACE",FACE,{"disambiguationData":[OSD([subQ0]),TDD([makeQuery(id+"F10.imprint","IMPRINT",EDGE,{"disambiguationData":[TD([[makeQuery(id+"F10.imprint","INTERSECT",VERTEX,{"derivedFrom":[sQuery(id+"F10.wireOp",EDGE,"E54"),subQ0]}),-1.0]])],"derivedFrom":subQ0})])]});}
            cPlane(context, id + "F12", {"entities" : qUnion([Q0]), "cplaneType" : CPlaneType.OFFSET, "offset" : 0 * mm, "width" : 150 * mm, "height" : 150 * mm});
        }
        {
            var Q0;
            Q0=makeQuery(id+"F1.opExtrude","SWEPT_BODY",BODY,{"disambiguationData":[OSD([sQuery(id+"F0.wireOp",EDGE,"E0.bottom"),sQuery(id+"F0.wireOp",EDGE,"E0.top"),sQuery(id+"F0.wireOp",EDGE,"E0.left"),sQuery(id+"F0.wireOp",EDGE,"E0.right"),sQuery(id+"F0.wireOp",EDGE,"E4"),sQuery(id+"F0.wireOp",EDGE,"E6"),sQuery(id+"F0.wireOp",EDGE,"E7"),sQuery(id+"F0.wireOp",EDGE,"E8"),sQuery(id+"F0.wireOp",EDGE,"E11"),sQuery(id+"F0.wireOp",EDGE,"E12"),sQuery(id+"F0.wireOp",EDGE,"E19.top"),sQuery(id+"F0.wireOp",EDGE,"E19.left"),sQuery(id+"F0.wireOp",EDGE,"E19.right"),sQuery(id+"F0.wireOp",EDGE,"E20.top"),sQuery(id+"F0.wireOp",EDGE,"E20.left"),sQuery(id+"F0.wireOp",EDGE,"E20.right"),sQuery(id+"F0.wireOp",EDGE,"E22"),sQuery(id+"F0.wireOp",EDGE,"E23")])]});
            var Q1;
            Q1=qCreatedBy(id+"F12.planeOp",FACE);
            mirror(context, id + "F13", {"operationType" : NewBodyOperationType.ADD, "entities" : qUnion([Q0]), "mirrorPlane" : qUnion([Q1])});
        }
    });
